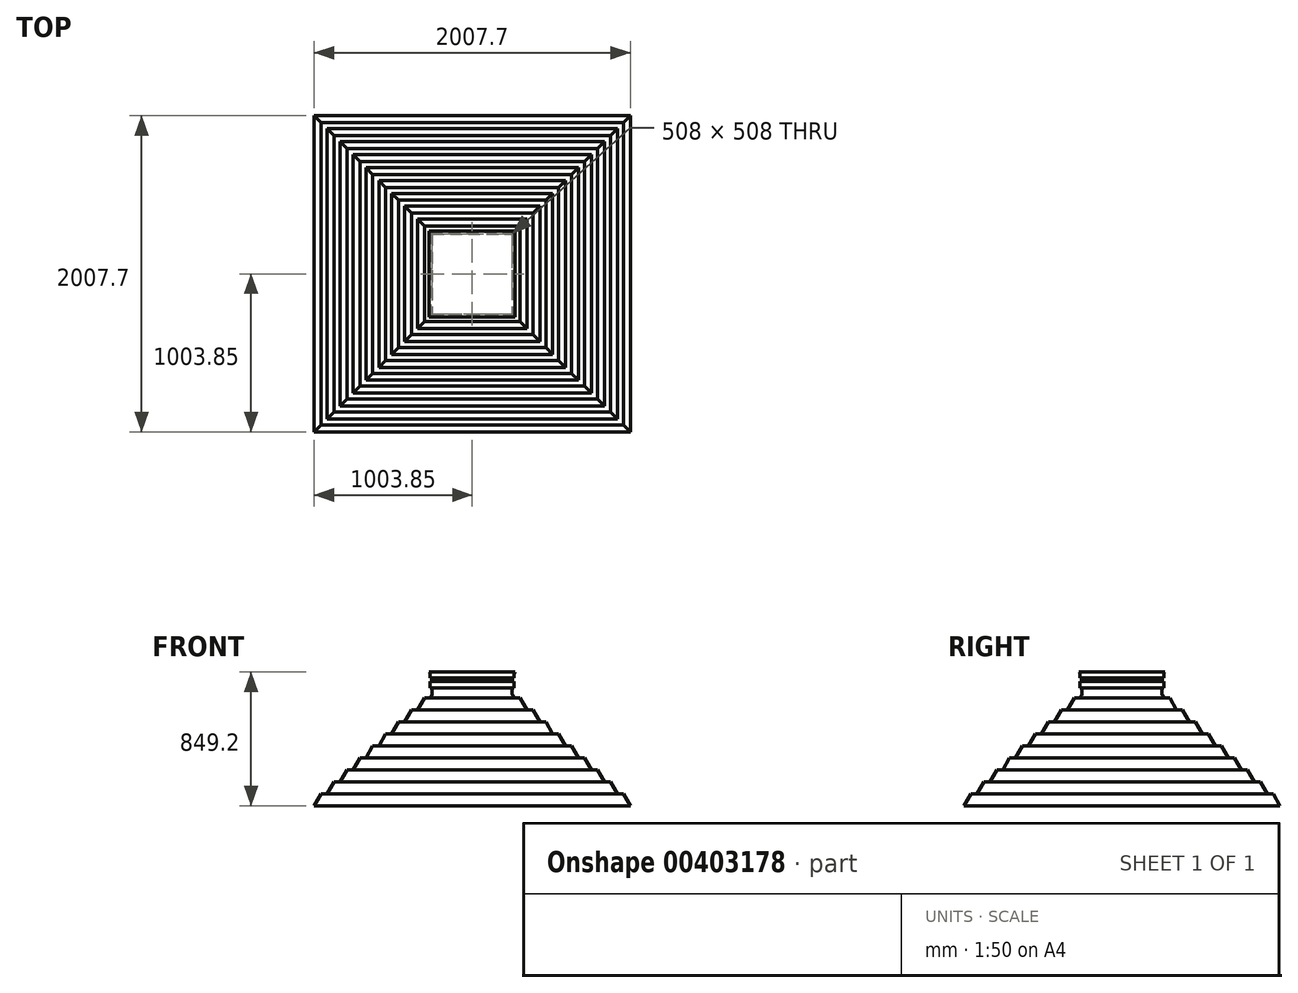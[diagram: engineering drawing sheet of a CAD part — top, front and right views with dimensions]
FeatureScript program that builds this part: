
annotation { "Feature Type Name" : "Feature", "Feature Type Description" : "" }
export const myFeature = defineFeature(function(context is Context, id is Id, definition is map)
    precondition{}
    {
        {
            var Q0;
            Q0=qCreatedBy(makeId("Front.planeOp"),FACE);
            var sketch = newSketch(context, id + "F0", { "sketchPlane" : qUnion([Q0])});
            skLineSegment(sketch, "E0", {"start": v(-254, 387.76) * mm, "end": v(-254, 363.24) * mm});
            skLineSegment(sketch, "E1", {"start": v(-265, 261.2) * mm, "end": v(265, 261.2) * mm});
            skLineSegment(sketch, "E2", {"start": v(254, 283.65) * mm, "end": v(254, 324.48) * mm});
            skLineSegment(sketch, "E3", {"start": v(-266.7, 337.4) * mm, "end": v(266.7, 337.4) * mm});
            skLineSegment(sketch, "E4", {"start": v(-266.7, 363.24) * mm, "end": v(266.7, 363.24) * mm});
            skLineSegment(sketch, "E5", {"start": v(-266.7, 354.13) * mm, "end": v(-266.7, 363.24) * mm});
            skLineSegment(sketch, "E6", {"start": v(-266.7, 350.32) * mm, "end": v(266.7, 350.32) * mm});
            skLineSegment(sketch, "E7", {"start": v(-254, 324.48) * mm, "end": v(-254, 283.65) * mm});
            skLineSegment(sketch, "E8", {"start": v(254, 363.24) * mm, "end": v(254, 387.76) * mm});
            skLineSegment(sketch, "E9", {"start": v(-266.7, 387.76) * mm, "end": v(266.7, 387.76) * mm});
            skLineSegment(sketch, "E10", {"start": v(-266.7, 387.76) * mm, "end": v(-266.7, 404.49) * mm});
            skLineSegment(sketch, "E11", {"start": v(266.7, 387.76) * mm, "end": v(266.7, 404.49) * mm});
            skLineSegment(sketch, "E12", {"start": v(-266.7, 400.68) * mm, "end": v(266.7, 400.68) * mm});
            skLineSegment(sketch, "E13", {"start": v(266.7, 404.49) * mm, "end": v(266.7, 411.9) * mm});
            skLineSegment(sketch, "E14", {"start": v(-266.7, 404.49) * mm, "end": v(-266.7, 411.9) * mm});
            skLineSegment(sketch, "E15", {"start": v(266.7, 354.13) * mm, "end": v(266.7, 363.24) * mm});
            skLineSegment(sketch, "E16", {"start": v(-255.7, 277.3) * mm, "end": v(-265, 261.2) * mm});
            skLineSegment(sketch, "E17", {"start": v(255.7, 277.3) * mm, "end": v(265, 261.2) * mm});
            skArc(sketch, "E18", {"start": v(-255.7, 277.3) * mm, "mid": v(-254.43, 280.37) * mm, "end": v(-254, 283.65) * mm});
            skArc(sketch, "E19", {"start": v(254, 283.65) * mm, "mid": v(254.43, 280.37) * mm, "end": v(255.7, 277.3) * mm});
            skLineSegment(sketch, "E20", {"start": v(0, 312) * mm, "end": v(76.2, 312) * mm});
            skLineSegment(sketch, "E21", {"start": v(76.2, 312) * mm, "end": v(76.2, 261.2) * mm});
            skLineSegment(sketch, "E22", {"start": v(0, 312) * mm, "end": v(-76.2, 312) * mm});
            skLineSegment(sketch, "E23", {"start": v(-76.2, 312) * mm, "end": v(-76.2, 261.2) * mm});
            skLineSegment(sketch, "E24", {"start": v(-38.1, 305.65) * mm, "end": v(-38.1, 261.2) * mm});
            skLineSegment(sketch, "E25", {"start": v(38.1, 305.65) * mm, "end": v(38.1, 261.2) * mm});
            skLineSegment(sketch, "E26", {"start": v(50.8, 305.65) * mm, "end": v(50.8, 261.2) * mm});
            skLineSegment(sketch, "E27", {"start": v(-50.8, 305.65) * mm, "end": v(-50.8, 261.2) * mm});
            skLineSegment(sketch, "E28", {"start": v(-303.1, 261.2) * mm, "end": v(-265, 261.2) * mm});
            skLineSegment(sketch, "E29", {"start": v(303.1, 261.2) * mm, "end": v(265, 261.2) * mm});
            skLineSegment(sketch, "E30", {"start": v(-549.38, 32.6) * mm, "end": v(-101.6, 32.6) * mm});
            skLineSegment(sketch, "E31", {"start": v(-631.47, -43.6) * mm, "end": v(-101.6, -43.6) * mm});
            skLineSegment(sketch, "E32", {"start": v(-303.1, 261.2) * mm, "end": v(-347.1, 185) * mm});
            skLineSegment(sketch, "E33", {"start": v(-385.2, 185) * mm, "end": v(-429.19, 108.8) * mm});
            skLineSegment(sketch, "E34", {"start": v(-467.29, 108.8) * mm, "end": v(-511.28, 32.6) * mm});
            skLineSegment(sketch, "E35", {"start": v(-549.38, 32.6) * mm, "end": v(-593.37, -43.6) * mm});
            skLineSegment(sketch, "E36", {"start": v(-631.47, -43.6) * mm, "end": v(-675.47, -119.8) * mm});
            skLineSegment(sketch, "E37", {"start": v(-713.57, -119.8) * mm, "end": v(-757.56, -196) * mm});
            skLineSegment(sketch, "E38", {"start": v(-795.66, -196) * mm, "end": v(-839.66, -272.2) * mm});
            skLineSegment(sketch, "E39", {"start": v(-877.76, -272.2) * mm, "end": v(-921.75, -348.4) * mm});
            skLineSegment(sketch, "E40", {"start": v(-959.85, -348.4) * mm, "end": v(-1003.85, -424.6) * mm});
            skLineSegment(sketch, "E41", {"start": v(303.1, 261.2) * mm, "end": v(347.1, 185) * mm});
            skLineSegment(sketch, "E42", {"start": v(385.2, 185) * mm, "end": v(429.19, 108.8) * mm});
            skLineSegment(sketch, "E43", {"start": v(467.29, 108.8) * mm, "end": v(511.28, 32.6) * mm});
            skLineSegment(sketch, "E44", {"start": v(549.38, 32.6) * mm, "end": v(593.37, -43.6) * mm});
            skLineSegment(sketch, "E45", {"start": v(631.47, -43.6) * mm, "end": v(675.47, -119.8) * mm});
            skLineSegment(sketch, "E46", {"start": v(713.57, -119.8) * mm, "end": v(757.56, -196) * mm});
            skLineSegment(sketch, "E47", {"start": v(795.66, -196) * mm, "end": v(839.66, -272.2) * mm});
            skLineSegment(sketch, "E48", {"start": v(877.76, -272.2) * mm, "end": v(921.75, -348.4) * mm});
            skLineSegment(sketch, "E49", {"start": v(959.85, -348.4) * mm, "end": v(1003.85, -424.6) * mm});
            skLineSegment(sketch, "E50", {"start": v(-959.85, -348.4) * mm, "end": v(-101.6, -348.4) * mm});
            skLineSegment(sketch, "E51", {"start": v(-795.66, -196) * mm, "end": v(-101.6, -196) * mm});
            skLineSegment(sketch, "E52", {"start": v(-877.76, -272.2) * mm, "end": v(-101.6, -272.2) * mm});
            skLineSegment(sketch, "E53", {"start": v(-713.57, -119.8) * mm, "end": v(-101.6, -119.8) * mm});
            skLineSegment(sketch, "E54", {"start": v(-385.2, 185) * mm, "end": v(-101.6, 185) * mm});
            skLineSegment(sketch, "E55", {"start": v(-467.29, 108.8) * mm, "end": v(-101.6, 108.8) * mm});
            skLineSegment(sketch, "E56", {"start": v(-870, -399.2) * mm, "end": v(-870, -361.1) * mm});
            skLineSegment(sketch, "E57", {"start": v(-736.15, -399.2) * mm, "end": v(-736.15, -361.1) * mm});
            skLineSegment(sketch, "E58", {"start": v(-602.3, -399.2) * mm, "end": v(-602.3, -361.1) * mm});
            skLineSegment(sketch, "E59", {"start": v(-870, -361.1) * mm, "end": v(-736.15, -361.1) * mm});
            skLineSegment(sketch, "E60", {"start": v(-989.18, -399.2) * mm, "end": v(-870, -399.2) * mm});
            skLineSegment(sketch, "E61", {"start": v(-736.15, -399.2) * mm, "end": v(-602.3, -399.2) * mm});
            skLineSegment(sketch, "E62", {"start": v(-602.3, -361.1) * mm, "end": v(-468.46, -361.1) * mm});
            skLineSegment(sketch, "E63", {"start": v(-468.46, -399.2) * mm, "end": v(-334.62, -399.2) * mm});
            skLineSegment(sketch, "E64", {"start": v(-334.62, -361.1) * mm, "end": v(-200.77, -361.1) * mm});
            skLineSegment(sketch, "E65", {"start": v(101.6, -399.2) * mm, "end": v(200.77, -399.2) * mm});
            skLineSegment(sketch, "E66", {"start": v(200.77, -361.1) * mm, "end": v(334.62, -361.1) * mm});
            skLineSegment(sketch, "E67", {"start": v(870, -399.2) * mm, "end": v(989.18, -399.2) * mm});
            skLineSegment(sketch, "E68", {"start": v(736.15, -361.1) * mm, "end": v(870, -361.1) * mm});
            skLineSegment(sketch, "E69", {"start": v(602.3, -399.2) * mm, "end": v(736.15, -399.2) * mm});
            skLineSegment(sketch, "E70", {"start": v(468.46, -361.1) * mm, "end": v(602.3, -361.1) * mm});
            skLineSegment(sketch, "E71", {"start": v(-1003.85, -424.6) * mm, "end": v(76.2, -424.6) * mm});
            skLineSegment(sketch, "E72", {"start": v(-468.46, -399.2) * mm, "end": v(-468.46, -361.1) * mm});
            skLineSegment(sketch, "E73", {"start": v(-334.62, -399.2) * mm, "end": v(-334.62, -361.1) * mm});
            skLineSegment(sketch, "E74", {"start": v(-200.77, -399.2) * mm, "end": v(-200.77, -361.1) * mm});
            skLineSegment(sketch, "E75", {"start": v(-200.77, -399.2) * mm, "end": v(-101.6, -399.2) * mm});
            skLineSegment(sketch, "E76", {"start": v(200.77, -399.2) * mm, "end": v(200.77, -361.1) * mm});
            skLineSegment(sketch, "E77", {"start": v(334.62, -399.2) * mm, "end": v(468.46, -399.2) * mm});
            skLineSegment(sketch, "E78", {"start": v(334.62, -399.2) * mm, "end": v(334.62, -361.1) * mm});
            skLineSegment(sketch, "E79", {"start": v(468.46, -399.2) * mm, "end": v(468.46, -361.1) * mm});
            skLineSegment(sketch, "E80", {"start": v(602.3, -399.2) * mm, "end": v(602.3, -361.1) * mm});
            skLineSegment(sketch, "E81", {"start": v(736.15, -399.2) * mm, "end": v(736.15, -361.1) * mm});
            skLineSegment(sketch, "E82", {"start": v(870, -361.1) * mm, "end": v(870, -399.2) * mm});
            skLineSegment(sketch, "E83", {"start": v(101.6, -348.4) * mm, "end": v(959.85, -348.4) * mm});
            skLineSegment(sketch, "E84", {"start": v(101.6, -272.2) * mm, "end": v(877.76, -272.2) * mm});
            skLineSegment(sketch, "E85", {"start": v(101.6, -196) * mm, "end": v(795.66, -196) * mm});
            skLineSegment(sketch, "E86", {"start": v(101.6, -119.8) * mm, "end": v(713.57, -119.8) * mm});
            skLineSegment(sketch, "E87", {"start": v(101.6, -43.6) * mm, "end": v(631.47, -43.6) * mm});
            skLineSegment(sketch, "E88", {"start": v(101.6, 32.6) * mm, "end": v(549.38, 32.6) * mm});
            skLineSegment(sketch, "E89", {"start": v(101.6, 108.8) * mm, "end": v(467.29, 108.8) * mm});
            skLineSegment(sketch, "E90", {"start": v(101.6, 185) * mm, "end": v(385.2, 185) * mm});
            skLineSegment(sketch, "E91", {"start": v(-292.38, 248.5) * mm, "end": v(-247.41, 248.5) * mm});
            skLineSegment(sketch, "E92", {"start": v(-202.44, 248.5) * mm, "end": v(-157.47, 248.5) * mm});
            skLineSegment(sketch, "E93", {"start": v(-112.5, 248.5) * mm, "end": v(-101.6, 248.5) * mm});
            skLineSegment(sketch, "E94", {"start": v(101.6, 248.5) * mm, "end": v(112.37, 248.5) * mm});
            skLineSegment(sketch, "E95", {"start": v(157.34, 248.5) * mm, "end": v(202.31, 248.5) * mm});
            skLineSegment(sketch, "E96", {"start": v(247.28, 248.5) * mm, "end": v(292.26, 248.5) * mm});
            skLineSegment(sketch, "E97", {"start": v(-292.38, 210.4) * mm, "end": v(-292.38, 248.5) * mm});
            skLineSegment(sketch, "E98", {"start": v(-247.41, 210.4) * mm, "end": v(-247.41, 248.5) * mm});
            skLineSegment(sketch, "E99", {"start": v(-202.44, 210.4) * mm, "end": v(-202.44, 248.5) * mm});
            skLineSegment(sketch, "E100", {"start": v(-157.47, 210.4) * mm, "end": v(-157.47, 248.5) * mm});
            skLineSegment(sketch, "E101", {"start": v(-112.5, 210.4) * mm, "end": v(-112.5, 248.5) * mm});
            skLineSegment(sketch, "E102", {"start": v(112.37, 210.4) * mm, "end": v(112.37, 248.5) * mm});
            skLineSegment(sketch, "E103", {"start": v(157.34, 210.4) * mm, "end": v(157.34, 248.5) * mm});
            skLineSegment(sketch, "E104", {"start": v(202.31, 210.4) * mm, "end": v(202.31, 248.5) * mm});
            skLineSegment(sketch, "E105", {"start": v(247.28, 210.4) * mm, "end": v(247.28, 248.5) * mm});
            skLineSegment(sketch, "E106", {"start": v(-332.43, 210.4) * mm, "end": v(-292.38, 210.4) * mm});
            skLineSegment(sketch, "E107", {"start": v(-247.41, 210.4) * mm, "end": v(-202.44, 210.4) * mm});
            skLineSegment(sketch, "E108", {"start": v(-157.47, 210.4) * mm, "end": v(-112.5, 210.4) * mm});
            skLineSegment(sketch, "E109", {"start": v(202.31, 210.4) * mm, "end": v(247.28, 210.4) * mm});
            skLineSegment(sketch, "E110", {"start": v(292.26, 210.4) * mm, "end": v(332.3, 210.4) * mm});
            skLineSegment(sketch, "E111", {"start": v(112.37, 210.4) * mm, "end": v(157.34, 210.4) * mm});
            skLineSegment(sketch, "E112", {"start": v(292.26, 248.5) * mm, "end": v(292.26, 210.4) * mm});
            skLineSegment(sketch, "E113", {"start": v(-364.59, 172.3) * mm, "end": v(-308.5, 172.3) * mm});
            skLineSegment(sketch, "E114", {"start": v(-252.42, 172.3) * mm, "end": v(-196.34, 172.3) * mm});
            skLineSegment(sketch, "E115", {"start": v(-140.26, 172.3) * mm, "end": v(-101.6, 172.3) * mm});
            skLineSegment(sketch, "E116", {"start": v(101.6, 172.3) * mm, "end": v(140.15, 172.3) * mm});
            skLineSegment(sketch, "E117", {"start": v(196.23, 172.3) * mm, "end": v(252.31, 172.3) * mm});
            skLineSegment(sketch, "E118", {"start": v(308.4, 172.3) * mm, "end": v(364.47, 172.3) * mm});
            skLineSegment(sketch, "E119", {"start": v(-364.59, 134.2) * mm, "end": v(-364.59, 172.3) * mm});
            skLineSegment(sketch, "E120", {"start": v(-308.5, 134.2) * mm, "end": v(-308.5, 172.3) * mm});
            skLineSegment(sketch, "E121", {"start": v(-252.42, 134.2) * mm, "end": v(-252.42, 172.3) * mm});
            skLineSegment(sketch, "E122", {"start": v(-196.34, 134.2) * mm, "end": v(-196.34, 172.3) * mm});
            skLineSegment(sketch, "E123", {"start": v(-140.26, 134.2) * mm, "end": v(-140.26, 172.3) * mm});
            skLineSegment(sketch, "E124", {"start": v(140.15, 134.2) * mm, "end": v(140.15, 172.3) * mm});
            skLineSegment(sketch, "E125", {"start": v(196.23, 134.2) * mm, "end": v(196.23, 172.3) * mm});
            skLineSegment(sketch, "E126", {"start": v(252.31, 134.2) * mm, "end": v(252.31, 172.3) * mm});
            skLineSegment(sketch, "E127", {"start": v(308.4, 134.2) * mm, "end": v(308.4, 172.3) * mm});
            skLineSegment(sketch, "E128", {"start": v(-414.52, 134.2) * mm, "end": v(-364.59, 134.2) * mm});
            skLineSegment(sketch, "E129", {"start": v(-308.5, 134.2) * mm, "end": v(-252.42, 134.2) * mm});
            skLineSegment(sketch, "E130", {"start": v(-196.34, 134.2) * mm, "end": v(-140.26, 134.2) * mm});
            skLineSegment(sketch, "E131", {"start": v(252.31, 134.2) * mm, "end": v(308.4, 134.2) * mm});
            skLineSegment(sketch, "E132", {"start": v(364.47, 134.2) * mm, "end": v(414.41, 134.2) * mm});
            skLineSegment(sketch, "E133", {"start": v(140.15, 134.2) * mm, "end": v(196.23, 134.2) * mm});
            skLineSegment(sketch, "E134", {"start": v(364.47, 172.3) * mm, "end": v(364.47, 134.2) * mm});
            skLineSegment(sketch, "E135", {"start": v(-436.79, 96.1) * mm, "end": v(-369.6, 96.1) * mm});
            skLineSegment(sketch, "E136", {"start": v(-302.4, 96.1) * mm, "end": v(-235.21, 96.1) * mm});
            skLineSegment(sketch, "E137", {"start": v(-168.02, 96.1) * mm, "end": v(-101.6, 96.1) * mm});
            skLineSegment(sketch, "E138", {"start": v(101.6, 96.1) * mm, "end": v(167.93, 96.1) * mm});
            skLineSegment(sketch, "E139", {"start": v(235.12, 96.1) * mm, "end": v(302.31, 96.1) * mm});
            skLineSegment(sketch, "E140", {"start": v(369.5, 96.1) * mm, "end": v(436.7, 96.1) * mm});
            skLineSegment(sketch, "E141", {"start": v(-436.79, 58) * mm, "end": v(-436.79, 96.1) * mm});
            skLineSegment(sketch, "E142", {"start": v(-369.6, 58) * mm, "end": v(-369.6, 96.1) * mm});
            skLineSegment(sketch, "E143", {"start": v(-302.4, 58) * mm, "end": v(-302.4, 96.1) * mm});
            skLineSegment(sketch, "E144", {"start": v(-235.21, 58) * mm, "end": v(-235.21, 96.1) * mm});
            skLineSegment(sketch, "E145", {"start": v(-168.02, 58) * mm, "end": v(-168.02, 96.1) * mm});
            skLineSegment(sketch, "E146", {"start": v(167.93, 58) * mm, "end": v(167.93, 96.1) * mm});
            skLineSegment(sketch, "E147", {"start": v(235.12, 58) * mm, "end": v(235.12, 96.1) * mm});
            skLineSegment(sketch, "E148", {"start": v(302.31, 58) * mm, "end": v(302.31, 96.1) * mm});
            skLineSegment(sketch, "E149", {"start": v(369.5, 58) * mm, "end": v(369.5, 96.1) * mm});
            skLineSegment(sketch, "E150", {"start": v(-496.62, 58) * mm, "end": v(-436.79, 58) * mm});
            skLineSegment(sketch, "E151", {"start": v(-369.6, 58) * mm, "end": v(-302.4, 58) * mm});
            skLineSegment(sketch, "E152", {"start": v(-235.21, 58) * mm, "end": v(-168.02, 58) * mm});
            skLineSegment(sketch, "E153", {"start": v(302.31, 58) * mm, "end": v(369.5, 58) * mm});
            skLineSegment(sketch, "E154", {"start": v(436.7, 58) * mm, "end": v(496.52, 58) * mm});
            skLineSegment(sketch, "E155", {"start": v(167.93, 58) * mm, "end": v(235.12, 58) * mm});
            skLineSegment(sketch, "E156", {"start": v(436.7, 96.1) * mm, "end": v(436.7, 58) * mm});
            skLineSegment(sketch, "E157", {"start": v(-508.99, 19.9) * mm, "end": v(-430.69, 19.9) * mm});
            skLineSegment(sketch, "E158", {"start": v(-352.39, 19.9) * mm, "end": v(-274.09, 19.9) * mm});
            skLineSegment(sketch, "E159", {"start": v(-195.79, 19.9) * mm, "end": v(-117.49, 19.9) * mm});
            skLineSegment(sketch, "E160", {"start": v(117.41, 19.9) * mm, "end": v(195.71, 19.9) * mm});
            skLineSegment(sketch, "E161", {"start": v(274.01, 19.9) * mm, "end": v(352.31, 19.9) * mm});
            skLineSegment(sketch, "E162", {"start": v(430.61, 19.9) * mm, "end": v(508.91, 19.9) * mm});
            skLineSegment(sketch, "E163", {"start": v(-508.99, -18.2) * mm, "end": v(-508.99, 19.9) * mm});
            skLineSegment(sketch, "E164", {"start": v(-430.69, -18.2) * mm, "end": v(-430.69, 19.9) * mm});
            skLineSegment(sketch, "E165", {"start": v(-352.39, -18.2) * mm, "end": v(-352.39, 19.9) * mm});
            skLineSegment(sketch, "E166", {"start": v(-274.09, -18.2) * mm, "end": v(-274.09, 19.9) * mm});
            skLineSegment(sketch, "E167", {"start": v(-195.79, -18.2) * mm, "end": v(-195.79, 19.9) * mm});
            skLineSegment(sketch, "E168", {"start": v(-117.49, -18.2) * mm, "end": v(-117.49, 19.9) * mm});
            skLineSegment(sketch, "E169", {"start": v(117.41, -18.2) * mm, "end": v(117.41, 19.9) * mm});
            skLineSegment(sketch, "E170", {"start": v(195.71, -18.2) * mm, "end": v(195.71, 19.9) * mm});
            skLineSegment(sketch, "E171", {"start": v(274.01, -18.2) * mm, "end": v(274.01, 19.9) * mm});
            skLineSegment(sketch, "E172", {"start": v(352.31, -18.2) * mm, "end": v(352.31, 19.9) * mm});
            skLineSegment(sketch, "E173", {"start": v(430.61, -18.2) * mm, "end": v(430.61, 19.9) * mm});
            skLineSegment(sketch, "E174", {"start": v(-578.71, -18.2) * mm, "end": v(-508.99, -18.2) * mm});
            skLineSegment(sketch, "E175", {"start": v(-430.69, -18.2) * mm, "end": v(-352.39, -18.2) * mm});
            skLineSegment(sketch, "E176", {"start": v(-274.09, -18.2) * mm, "end": v(-195.79, -18.2) * mm});
            skLineSegment(sketch, "E177", {"start": v(-117.49, -18.2) * mm, "end": v(-101.6, -18.2) * mm});
            skLineSegment(sketch, "E178", {"start": v(101.6, -18.2) * mm, "end": v(117.41, -18.2) * mm});
            skLineSegment(sketch, "E179", {"start": v(352.31, -18.2) * mm, "end": v(430.61, -18.2) * mm});
            skLineSegment(sketch, "E180", {"start": v(508.91, -18.2) * mm, "end": v(578.63, -18.2) * mm});
            skLineSegment(sketch, "E181", {"start": v(195.71, -18.2) * mm, "end": v(274.01, -18.2) * mm});
            skLineSegment(sketch, "E182", {"start": v(508.91, 19.9) * mm, "end": v(508.91, -18.2) * mm});
            skLineSegment(sketch, "E183", {"start": v(-581.2, -56.3) * mm, "end": v(-491.78, -56.3) * mm});
            skLineSegment(sketch, "E184", {"start": v(-402.37, -56.3) * mm, "end": v(-312.96, -56.3) * mm});
            skLineSegment(sketch, "E185", {"start": v(-223.55, -56.3) * mm, "end": v(-134.15, -56.3) * mm});
            skLineSegment(sketch, "E186", {"start": v(134.08, -56.3) * mm, "end": v(223.5, -56.3) * mm});
            skLineSegment(sketch, "E187", {"start": v(312.9, -56.3) * mm, "end": v(402.3, -56.3) * mm});
            skLineSegment(sketch, "E188", {"start": v(491.72, -56.3) * mm, "end": v(581.13, -56.3) * mm});
            skLineSegment(sketch, "E189", {"start": v(-581.2, -94.4) * mm, "end": v(-581.2, -56.3) * mm});
            skLineSegment(sketch, "E190", {"start": v(-491.78, -94.4) * mm, "end": v(-491.78, -56.3) * mm});
            skLineSegment(sketch, "E191", {"start": v(-402.37, -94.4) * mm, "end": v(-402.37, -56.3) * mm});
            skLineSegment(sketch, "E192", {"start": v(-312.96, -94.4) * mm, "end": v(-312.96, -56.3) * mm});
            skLineSegment(sketch, "E193", {"start": v(-223.55, -94.4) * mm, "end": v(-223.55, -56.3) * mm});
            skLineSegment(sketch, "E194", {"start": v(-134.15, -94.4) * mm, "end": v(-134.15, -56.3) * mm});
            skLineSegment(sketch, "E195", {"start": v(134.08, -94.4) * mm, "end": v(134.08, -56.3) * mm});
            skLineSegment(sketch, "E196", {"start": v(223.5, -94.4) * mm, "end": v(223.5, -56.3) * mm});
            skLineSegment(sketch, "E197", {"start": v(312.9, -94.4) * mm, "end": v(312.9, -56.3) * mm});
            skLineSegment(sketch, "E198", {"start": v(402.3, -94.4) * mm, "end": v(402.3, -56.3) * mm});
            skLineSegment(sketch, "E199", {"start": v(491.72, -94.4) * mm, "end": v(491.72, -56.3) * mm});
            skLineSegment(sketch, "E200", {"start": v(-660.8, -94.4) * mm, "end": v(-581.2, -94.4) * mm});
            skLineSegment(sketch, "E201", {"start": v(-491.78, -94.4) * mm, "end": v(-402.37, -94.4) * mm});
            skLineSegment(sketch, "E202", {"start": v(-312.96, -94.4) * mm, "end": v(-223.55, -94.4) * mm});
            skLineSegment(sketch, "E203", {"start": v(-134.15, -94.4) * mm, "end": v(-101.6, -94.4) * mm});
            skLineSegment(sketch, "E204", {"start": v(101.6, -94.4) * mm, "end": v(134.08, -94.4) * mm});
            skLineSegment(sketch, "E205", {"start": v(402.3, -94.4) * mm, "end": v(491.72, -94.4) * mm});
            skLineSegment(sketch, "E206", {"start": v(581.13, -94.4) * mm, "end": v(660.74, -94.4) * mm});
            skLineSegment(sketch, "E207", {"start": v(223.5, -94.4) * mm, "end": v(312.9, -94.4) * mm});
            skLineSegment(sketch, "E208", {"start": v(581.13, -56.3) * mm, "end": v(581.13, -94.4) * mm});
            skLineSegment(sketch, "E209", {"start": v(-653.4, -132.5) * mm, "end": v(-552.87, -132.5) * mm});
            skLineSegment(sketch, "E210", {"start": v(-452.36, -132.5) * mm, "end": v(-351.84, -132.5) * mm});
            skLineSegment(sketch, "E211", {"start": v(-251.32, -132.5) * mm, "end": v(-150.8, -132.5) * mm});
            skLineSegment(sketch, "E212", {"start": v(150.75, -132.5) * mm, "end": v(251.27, -132.5) * mm});
            skLineSegment(sketch, "E213", {"start": v(351.8, -132.5) * mm, "end": v(452.3, -132.5) * mm});
            skLineSegment(sketch, "E214", {"start": v(552.83, -132.5) * mm, "end": v(653.35, -132.5) * mm});
            skLineSegment(sketch, "E215", {"start": v(-653.4, -170.6) * mm, "end": v(-653.4, -132.5) * mm});
            skLineSegment(sketch, "E216", {"start": v(-552.87, -170.6) * mm, "end": v(-552.87, -132.5) * mm});
            skLineSegment(sketch, "E217", {"start": v(-452.36, -170.6) * mm, "end": v(-452.36, -132.5) * mm});
            skLineSegment(sketch, "E218", {"start": v(-351.84, -170.6) * mm, "end": v(-351.84, -132.5) * mm});
            skLineSegment(sketch, "E219", {"start": v(-251.32, -170.6) * mm, "end": v(-251.32, -132.5) * mm});
            skLineSegment(sketch, "E220", {"start": v(-150.8, -170.6) * mm, "end": v(-150.8, -132.5) * mm});
            skLineSegment(sketch, "E221", {"start": v(150.75, -170.6) * mm, "end": v(150.75, -132.5) * mm});
            skLineSegment(sketch, "E222", {"start": v(251.27, -170.6) * mm, "end": v(251.27, -132.5) * mm});
            skLineSegment(sketch, "E223", {"start": v(351.8, -170.6) * mm, "end": v(351.8, -132.5) * mm});
            skLineSegment(sketch, "E224", {"start": v(452.3, -170.6) * mm, "end": v(452.3, -132.5) * mm});
            skLineSegment(sketch, "E225", {"start": v(552.83, -170.6) * mm, "end": v(552.83, -132.5) * mm});
            skLineSegment(sketch, "E226", {"start": v(-742.9, -170.6) * mm, "end": v(-653.4, -170.6) * mm});
            skLineSegment(sketch, "E227", {"start": v(-552.87, -170.6) * mm, "end": v(-452.36, -170.6) * mm});
            skLineSegment(sketch, "E228", {"start": v(-351.84, -170.6) * mm, "end": v(-251.32, -170.6) * mm});
            skLineSegment(sketch, "E229", {"start": v(-150.8, -170.6) * mm, "end": v(-101.6, -170.6) * mm});
            skLineSegment(sketch, "E230", {"start": v(101.6, -170.6) * mm, "end": v(150.75, -170.6) * mm});
            skLineSegment(sketch, "E231", {"start": v(452.3, -170.6) * mm, "end": v(552.83, -170.6) * mm});
            skLineSegment(sketch, "E232", {"start": v(653.35, -170.6) * mm, "end": v(742.85, -170.6) * mm});
            skLineSegment(sketch, "E233", {"start": v(251.27, -170.6) * mm, "end": v(351.8, -170.6) * mm});
            skLineSegment(sketch, "E234", {"start": v(653.35, -132.5) * mm, "end": v(653.35, -170.6) * mm});
            skLineSegment(sketch, "E235", {"start": v(-725.6, -208.7) * mm, "end": v(-613.97, -208.7) * mm});
            skLineSegment(sketch, "E236", {"start": v(-502.34, -208.7) * mm, "end": v(-390.71, -208.7) * mm});
            skLineSegment(sketch, "E237", {"start": v(-279.08, -208.7) * mm, "end": v(-167.46, -208.7) * mm});
            skLineSegment(sketch, "E238", {"start": v(167.43, -208.7) * mm, "end": v(279.05, -208.7) * mm});
            skLineSegment(sketch, "E239", {"start": v(390.68, -208.7) * mm, "end": v(502.3, -208.7) * mm});
            skLineSegment(sketch, "E240", {"start": v(613.94, -208.7) * mm, "end": v(725.56, -208.7) * mm});
            skLineSegment(sketch, "E241", {"start": v(-725.6, -246.8) * mm, "end": v(-725.6, -208.7) * mm});
            skLineSegment(sketch, "E242", {"start": v(-613.97, -246.8) * mm, "end": v(-613.97, -208.7) * mm});
            skLineSegment(sketch, "E243", {"start": v(-502.34, -246.8) * mm, "end": v(-502.34, -208.7) * mm});
            skLineSegment(sketch, "E244", {"start": v(-390.71, -246.8) * mm, "end": v(-390.71, -208.7) * mm});
            skLineSegment(sketch, "E245", {"start": v(-279.08, -246.8) * mm, "end": v(-279.08, -208.7) * mm});
            skLineSegment(sketch, "E246", {"start": v(-167.46, -246.8) * mm, "end": v(-167.46, -208.7) * mm});
            skLineSegment(sketch, "E247", {"start": v(167.43, -246.8) * mm, "end": v(167.43, -208.7) * mm});
            skLineSegment(sketch, "E248", {"start": v(279.05, -246.8) * mm, "end": v(279.05, -208.7) * mm});
            skLineSegment(sketch, "E249", {"start": v(390.68, -246.8) * mm, "end": v(390.68, -208.7) * mm});
            skLineSegment(sketch, "E250", {"start": v(502.3, -246.8) * mm, "end": v(502.3, -208.7) * mm});
            skLineSegment(sketch, "E251", {"start": v(613.94, -246.8) * mm, "end": v(613.94, -208.7) * mm});
            skLineSegment(sketch, "E252", {"start": v(-825, -246.8) * mm, "end": v(-725.6, -246.8) * mm});
            skLineSegment(sketch, "E253", {"start": v(-613.97, -246.8) * mm, "end": v(-502.34, -246.8) * mm});
            skLineSegment(sketch, "E254", {"start": v(-390.71, -246.8) * mm, "end": v(-279.08, -246.8) * mm});
            skLineSegment(sketch, "E255", {"start": v(-167.46, -246.8) * mm, "end": v(-101.6, -246.8) * mm});
            skLineSegment(sketch, "E256", {"start": v(101.6, -246.8) * mm, "end": v(167.43, -246.8) * mm});
            skLineSegment(sketch, "E257", {"start": v(502.3, -246.8) * mm, "end": v(613.94, -246.8) * mm});
            skLineSegment(sketch, "E258", {"start": v(725.56, -246.8) * mm, "end": v(824.96, -246.8) * mm});
            skLineSegment(sketch, "E259", {"start": v(279.05, -246.8) * mm, "end": v(390.68, -246.8) * mm});
            skLineSegment(sketch, "E260", {"start": v(725.56, -208.7) * mm, "end": v(725.56, -246.8) * mm});
            skLineSegment(sketch, "E261", {"start": v(-797.8, -284.9) * mm, "end": v(-675.06, -284.9) * mm});
            skLineSegment(sketch, "E262", {"start": v(-552.32, -284.9) * mm, "end": v(-429.59, -284.9) * mm});
            skLineSegment(sketch, "E263", {"start": v(-306.85, -284.9) * mm, "end": v(-184.11, -284.9) * mm});
            skLineSegment(sketch, "E264", {"start": v(184.1, -284.9) * mm, "end": v(306.83, -284.9) * mm});
            skLineSegment(sketch, "E265", {"start": v(429.57, -284.9) * mm, "end": v(552.3, -284.9) * mm});
            skLineSegment(sketch, "E266", {"start": v(675.04, -284.9) * mm, "end": v(797.78, -284.9) * mm});
            skLineSegment(sketch, "E267", {"start": v(-797.8, -323) * mm, "end": v(-797.8, -284.9) * mm});
            skLineSegment(sketch, "E268", {"start": v(-675.06, -323) * mm, "end": v(-675.06, -284.9) * mm});
            skLineSegment(sketch, "E269", {"start": v(-552.32, -323) * mm, "end": v(-552.32, -284.9) * mm});
            skLineSegment(sketch, "E270", {"start": v(-429.59, -323) * mm, "end": v(-429.59, -284.9) * mm});
            skLineSegment(sketch, "E271", {"start": v(-306.85, -323) * mm, "end": v(-306.85, -284.9) * mm});
            skLineSegment(sketch, "E272", {"start": v(-184.11, -323) * mm, "end": v(-184.11, -284.9) * mm});
            skLineSegment(sketch, "E273", {"start": v(184.1, -323) * mm, "end": v(184.1, -284.9) * mm});
            skLineSegment(sketch, "E274", {"start": v(306.83, -323) * mm, "end": v(306.83, -284.9) * mm});
            skLineSegment(sketch, "E275", {"start": v(429.57, -323) * mm, "end": v(429.57, -284.9) * mm});
            skLineSegment(sketch, "E276", {"start": v(552.3, -323) * mm, "end": v(552.3, -284.9) * mm});
            skLineSegment(sketch, "E277", {"start": v(675.04, -323) * mm, "end": v(675.04, -284.9) * mm});
            skLineSegment(sketch, "E278", {"start": v(-907.09, -323) * mm, "end": v(-797.8, -323) * mm});
            skLineSegment(sketch, "E279", {"start": v(-675.06, -323) * mm, "end": v(-552.32, -323) * mm});
            skLineSegment(sketch, "E280", {"start": v(-429.59, -323) * mm, "end": v(-306.85, -323) * mm});
            skLineSegment(sketch, "E281", {"start": v(-184.11, -323) * mm, "end": v(-101.6, -323) * mm});
            skLineSegment(sketch, "E282", {"start": v(101.6, -323) * mm, "end": v(184.1, -323) * mm});
            skLineSegment(sketch, "E283", {"start": v(552.3, -323) * mm, "end": v(675.04, -323) * mm});
            skLineSegment(sketch, "E284", {"start": v(797.78, -323) * mm, "end": v(907.07, -323) * mm});
            skLineSegment(sketch, "E285", {"start": v(306.83, -323) * mm, "end": v(429.57, -323) * mm});
            skLineSegment(sketch, "E286", {"start": v(797.78, -284.9) * mm, "end": v(797.78, -323) * mm});
            skLineSegment(sketch, "E287", {"start": v(-57.15, 312) * mm, "end": v(-57.15, 305.65) * mm});
            skLineSegment(sketch, "E288", {"start": v(-31.75, 312) * mm, "end": v(-31.75, 305.65) * mm});
            skLineSegment(sketch, "E289", {"start": v(31.75, 312) * mm, "end": v(31.75, 305.65) * mm});
            skLineSegment(sketch, "E290", {"start": v(57.15, 312) * mm, "end": v(57.15, 305.65) * mm});
            skLineSegment(sketch, "E291", {"start": v(38.1, 305.65) * mm, "end": v(31.75, 305.65) * mm});
            skLineSegment(sketch, "E292", {"start": v(-50.8, 305.65) * mm, "end": v(-57.15, 305.65) * mm});
            skLineSegment(sketch, "E293", {"start": v(57.15, 305.65) * mm, "end": v(50.8, 305.65) * mm});
            skLineSegment(sketch, "E294", {"start": v(-31.75, 305.65) * mm, "end": v(-38.1, 305.65) * mm});
            skLineSegment(sketch, "E295", {"start": v(-267.55, 415.07) * mm, "end": v(-273.05, 424.6) * mm});
            skLineSegment(sketch, "E296", {"start": v(267.55, 415.07) * mm, "end": v(273.05, 424.6) * mm});
            skLineSegment(sketch, "E297", {"start": v(273.05, 424.6) * mm, "end": v(-273.05, 424.6) * mm});
            skLineSegment(sketch, "E298", {"start": v(-266.7, 324.48) * mm, "end": v(266.7, 324.48) * mm});
            skLineSegment(sketch, "E299", {"start": v(-266.7, 354.13) * mm, "end": v(-266.7, 324.48) * mm});
            skLineSegment(sketch, "E300", {"start": v(-23.24, 381.85) * mm, "end": v(23.24, 381.85) * mm});
            skLineSegment(sketch, "E301", {"start": v(23.24, 381.85) * mm, "end": v(23.24, 369.15) * mm});
            skLineSegment(sketch, "E302", {"start": v(23.24, 369.15) * mm, "end": v(-23.24, 369.15) * mm});
            skLineSegment(sketch, "E303", {"start": v(-23.24, 381.85) * mm, "end": v(-23.24, 369.15) * mm});
            skLineSegment(sketch, "E304", {"start": v(180.6, 369.15) * mm, "end": v(180.6, 381.85) * mm});
            skLineSegment(sketch, "E305", {"start": v(-180.6, 381.85) * mm, "end": v(-180.6, 369.15) * mm});
            skLineSegment(sketch, "E306", {"start": v(-127.25, 381.85) * mm, "end": v(-127.25, 369.15) * mm});
            skLineSegment(sketch, "E307", {"start": v(127.25, 369.15) * mm, "end": v(127.25, 381.85) * mm});
            skLineSegment(sketch, "E308", {"start": v(-127.25, 381.85) * mm, "end": v(-180.6, 381.85) * mm});
            skLineSegment(sketch, "E309", {"start": v(-127.25, 369.15) * mm, "end": v(-180.6, 369.15) * mm});
            skLineSegment(sketch, "E310", {"start": v(127.25, 381.85) * mm, "end": v(180.6, 381.85) * mm});
            skLineSegment(sketch, "E311", {"start": v(127.25, 369.15) * mm, "end": v(180.6, 369.15) * mm});
            skLineSegment(sketch, "E312", {"start": v(-254, 283.65) * mm, "end": v(-76.2, 283.65) * mm});
            skLineSegment(sketch, "E313", {"start": v(-255.7, 277.3) * mm, "end": v(-76.2, 277.3) * mm});
            skLineSegment(sketch, "E314", {"start": v(254, 283.65) * mm, "end": v(76.2, 283.65) * mm});
            skLineSegment(sketch, "E315", {"start": v(255.7, 277.3) * mm, "end": v(76.2, 277.3) * mm});
            skLineSegment(sketch, "E316", {"start": v(266.7, 354.13) * mm, "end": v(266.7, 324.48) * mm});
            skArc(sketch, "E317", {"start": v(267.55, 415.07) * mm, "mid": v(266.92, 413.54) * mm, "end": v(266.7, 411.9) * mm});
            skArc(sketch, "E318", {"start": v(-266.7, 411.9) * mm, "mid": v(-266.92, 413.54) * mm, "end": v(-267.55, 415.07) * mm});
            skLineSegment(sketch, "E319", {"start": v(-266.7, 411.9) * mm, "end": v(266.7, 411.9) * mm});
            skLineSegment(sketch, "E320", {"start": v(267.55, 415.07) * mm, "end": v(-267.55, 415.07) * mm});
            skLineSegment(sketch, "E321", {"start": v(101.6, -424.6) * mm, "end": v(101.6, 261.2) * mm});
            skLineSegment(sketch, "E322", {"start": v(-101.6, -424.6) * mm, "end": v(-101.6, 261.2) * mm});
            skLineSegment(sketch, "E323", {"start": v(-76.2, -424.6) * mm, "end": v(-76.2, 261.2) * mm});
            skLineSegment(sketch, "E324", {"start": v(76.2, -424.6) * mm, "end": v(76.2, 261.2) * mm});
            skLineSegment(sketch, "E325", {"start": v(-76.2, 261.2) * mm, "end": v(50.8, 261.2) * mm});
            skLineSegment(sketch, "E326", {"start": v(50.8, 253.66) * mm, "end": v(76.2, 253.66) * mm});
            skLineSegment(sketch, "E327", {"start": v(-76.2, 253.66) * mm, "end": v(50.8, 253.66) * mm});
            skLineSegment(sketch, "E328", {"start": v(50.8, 246.11) * mm, "end": v(76.2, 246.11) * mm});
            skLineSegment(sketch, "E329", {"start": v(-76.2, 246.11) * mm, "end": v(50.8, 246.11) * mm});
            skLineSegment(sketch, "E330", {"start": v(50.8, 238.57) * mm, "end": v(76.2, 238.57) * mm});
            skLineSegment(sketch, "E331", {"start": v(-76.2, 238.57) * mm, "end": v(50.8, 238.57) * mm});
            skLineSegment(sketch, "E332", {"start": v(50.8, 231.03) * mm, "end": v(76.2, 231.03) * mm});
            skLineSegment(sketch, "E333", {"start": v(-76.2, 231.03) * mm, "end": v(50.8, 231.03) * mm});
            skLineSegment(sketch, "E334", {"start": v(50.8, 223.48) * mm, "end": v(76.2, 223.48) * mm});
            skLineSegment(sketch, "E335", {"start": v(-76.2, 223.48) * mm, "end": v(50.8, 223.48) * mm});
            skLineSegment(sketch, "E336", {"start": v(50.8, 215.94) * mm, "end": v(76.2, 215.94) * mm});
            skLineSegment(sketch, "E337", {"start": v(-76.2, 215.94) * mm, "end": v(50.8, 215.94) * mm});
            skLineSegment(sketch, "E338", {"start": v(50.8, 208.4) * mm, "end": v(76.2, 208.4) * mm});
            skLineSegment(sketch, "E339", {"start": v(-76.2, 208.4) * mm, "end": v(50.8, 208.4) * mm});
            skLineSegment(sketch, "E340", {"start": v(50.8, 200.85) * mm, "end": v(76.2, 200.85) * mm});
            skLineSegment(sketch, "E341", {"start": v(-76.2, 200.85) * mm, "end": v(50.8, 200.85) * mm});
            skLineSegment(sketch, "E342", {"start": v(50.8, 193.3) * mm, "end": v(76.2, 193.3) * mm});
            skLineSegment(sketch, "E343", {"start": v(-76.2, 193.3) * mm, "end": v(50.8, 193.3) * mm});
            skLineSegment(sketch, "E344", {"start": v(50.8, 185.76) * mm, "end": v(76.2, 185.76) * mm});
            skLineSegment(sketch, "E345", {"start": v(-76.2, 185.76) * mm, "end": v(50.8, 185.76) * mm});
            skLineSegment(sketch, "E346", {"start": v(50.8, 178.22) * mm, "end": v(76.2, 178.22) * mm});
            skLineSegment(sketch, "E347", {"start": v(-76.2, 178.22) * mm, "end": v(50.8, 178.22) * mm});
            skLineSegment(sketch, "E348", {"start": v(50.8, 170.68) * mm, "end": v(76.2, 170.68) * mm});
            skLineSegment(sketch, "E349", {"start": v(-76.2, 170.68) * mm, "end": v(50.8, 170.68) * mm});
            skLineSegment(sketch, "E350", {"start": v(50.8, 163.13) * mm, "end": v(76.2, 163.13) * mm});
            skLineSegment(sketch, "E351", {"start": v(-76.2, 163.13) * mm, "end": v(50.8, 163.13) * mm});
            skLineSegment(sketch, "E352", {"start": v(50.8, 155.59) * mm, "end": v(76.2, 155.59) * mm});
            skLineSegment(sketch, "E353", {"start": v(-76.2, 155.59) * mm, "end": v(50.8, 155.59) * mm});
            skLineSegment(sketch, "E354", {"start": v(50.8, 148.04) * mm, "end": v(76.2, 148.04) * mm});
            skLineSegment(sketch, "E355", {"start": v(-76.2, 148.04) * mm, "end": v(50.8, 148.04) * mm});
            skLineSegment(sketch, "E356", {"start": v(50.8, 140.5) * mm, "end": v(76.2, 140.5) * mm});
            skLineSegment(sketch, "E357", {"start": v(-76.2, 140.5) * mm, "end": v(50.8, 140.5) * mm});
            skLineSegment(sketch, "E358", {"start": v(50.8, 132.96) * mm, "end": v(76.2, 132.96) * mm});
            skLineSegment(sketch, "E359", {"start": v(-76.2, 132.96) * mm, "end": v(50.8, 132.96) * mm});
            skLineSegment(sketch, "E360", {"start": v(50.8, 125.41) * mm, "end": v(76.2, 125.41) * mm});
            skLineSegment(sketch, "E361", {"start": v(-76.2, 125.41) * mm, "end": v(50.8, 125.41) * mm});
            skLineSegment(sketch, "E362", {"start": v(50.8, 117.87) * mm, "end": v(76.2, 117.87) * mm});
            skLineSegment(sketch, "E363", {"start": v(-76.2, 117.87) * mm, "end": v(50.8, 117.87) * mm});
            skLineSegment(sketch, "E364", {"start": v(50.8, 110.32) * mm, "end": v(76.2, 110.32) * mm});
            skLineSegment(sketch, "E365", {"start": v(-76.2, 110.32) * mm, "end": v(50.8, 110.32) * mm});
            skLineSegment(sketch, "E366", {"start": v(50.8, 102.78) * mm, "end": v(76.2, 102.78) * mm});
            skLineSegment(sketch, "E367", {"start": v(-76.2, 102.78) * mm, "end": v(50.8, 102.78) * mm});
            skLineSegment(sketch, "E368", {"start": v(50.8, 95.24) * mm, "end": v(76.2, 95.24) * mm});
            skLineSegment(sketch, "E369", {"start": v(-76.2, 95.24) * mm, "end": v(50.8, 95.24) * mm});
            skLineSegment(sketch, "E370", {"start": v(50.8, 87.7) * mm, "end": v(76.2, 87.7) * mm});
            skLineSegment(sketch, "E371", {"start": v(-76.2, 87.7) * mm, "end": v(50.8, 87.7) * mm});
            skLineSegment(sketch, "E372", {"start": v(50.8, 80.15) * mm, "end": v(76.2, 80.15) * mm});
            skLineSegment(sketch, "E373", {"start": v(-76.2, 80.15) * mm, "end": v(50.8, 80.15) * mm});
            skLineSegment(sketch, "E374", {"start": v(50.8, 72.6) * mm, "end": v(76.2, 72.6) * mm});
            skLineSegment(sketch, "E375", {"start": v(-76.2, 72.6) * mm, "end": v(50.8, 72.6) * mm});
            skLineSegment(sketch, "E376", {"start": v(50.8, 65.06) * mm, "end": v(76.2, 65.06) * mm});
            skLineSegment(sketch, "E377", {"start": v(-76.2, 65.06) * mm, "end": v(50.8, 65.06) * mm});
            skLineSegment(sketch, "E378", {"start": v(50.8, 57.52) * mm, "end": v(76.2, 57.52) * mm});
            skLineSegment(sketch, "E379", {"start": v(-76.2, 57.52) * mm, "end": v(50.8, 57.52) * mm});
            skLineSegment(sketch, "E380", {"start": v(50.8, 49.97) * mm, "end": v(76.2, 49.97) * mm});
            skLineSegment(sketch, "E381", {"start": v(-76.2, 49.97) * mm, "end": v(50.8, 49.97) * mm});
            skLineSegment(sketch, "E382", {"start": v(50.8, 42.43) * mm, "end": v(76.2, 42.43) * mm});
            skLineSegment(sketch, "E383", {"start": v(-76.2, 42.43) * mm, "end": v(50.8, 42.43) * mm});
            skLineSegment(sketch, "E384", {"start": v(50.8, 34.89) * mm, "end": v(76.2, 34.89) * mm});
            skLineSegment(sketch, "E385", {"start": v(-76.2, 34.89) * mm, "end": v(50.8, 34.89) * mm});
            skLineSegment(sketch, "E386", {"start": v(50.8, 27.34) * mm, "end": v(76.2, 27.34) * mm});
            skLineSegment(sketch, "E387", {"start": v(-76.2, 27.34) * mm, "end": v(50.8, 27.34) * mm});
            skLineSegment(sketch, "E388", {"start": v(50.8, 19.8) * mm, "end": v(76.2, 19.8) * mm});
            skLineSegment(sketch, "E389", {"start": v(-76.2, 19.8) * mm, "end": v(50.8, 19.8) * mm});
            skLineSegment(sketch, "E390", {"start": v(50.8, 12.26) * mm, "end": v(76.2, 12.26) * mm});
            skLineSegment(sketch, "E391", {"start": v(-76.2, 12.26) * mm, "end": v(50.8, 12.26) * mm});
            skLineSegment(sketch, "E392", {"start": v(50.8, 4.71) * mm, "end": v(76.2, 4.71) * mm});
            skLineSegment(sketch, "E393", {"start": v(-76.2, 4.71) * mm, "end": v(50.8, 4.71) * mm});
            skLineSegment(sketch, "E394", {"start": v(50.8, -2.83) * mm, "end": v(76.2, -2.83) * mm});
            skLineSegment(sketch, "E395", {"start": v(-76.2, -2.83) * mm, "end": v(50.8, -2.83) * mm});
            skLineSegment(sketch, "E396", {"start": v(50.8, -10.38) * mm, "end": v(76.2, -10.38) * mm});
            skLineSegment(sketch, "E397", {"start": v(-76.2, -10.38) * mm, "end": v(50.8, -10.38) * mm});
            skLineSegment(sketch, "E398", {"start": v(50.8, -17.92) * mm, "end": v(76.2, -17.92) * mm});
            skLineSegment(sketch, "E399", {"start": v(-76.2, -17.92) * mm, "end": v(50.8, -17.92) * mm});
            skLineSegment(sketch, "E400", {"start": v(50.8, -25.46) * mm, "end": v(76.2, -25.46) * mm});
            skLineSegment(sketch, "E401", {"start": v(-76.2, -25.46) * mm, "end": v(50.8, -25.46) * mm});
            skLineSegment(sketch, "E402", {"start": v(50.8, -33) * mm, "end": v(76.2, -33) * mm});
            skLineSegment(sketch, "E403", {"start": v(-76.2, -33) * mm, "end": v(50.8, -33) * mm});
            skLineSegment(sketch, "E404", {"start": v(50.8, -40.55) * mm, "end": v(76.2, -40.55) * mm});
            skLineSegment(sketch, "E405", {"start": v(-76.2, -40.55) * mm, "end": v(50.8, -40.55) * mm});
            skLineSegment(sketch, "E406", {"start": v(50.8, -48.1) * mm, "end": v(76.2, -48.1) * mm});
            skLineSegment(sketch, "E407", {"start": v(-76.2, -48.1) * mm, "end": v(50.8, -48.1) * mm});
            skLineSegment(sketch, "E408", {"start": v(50.8, -55.64) * mm, "end": v(76.2, -55.64) * mm});
            skLineSegment(sketch, "E409", {"start": v(-76.2, -55.64) * mm, "end": v(50.8, -55.64) * mm});
            skLineSegment(sketch, "E410", {"start": v(50.8, -63.18) * mm, "end": v(76.2, -63.18) * mm});
            skLineSegment(sketch, "E411", {"start": v(-76.2, -63.18) * mm, "end": v(50.8, -63.18) * mm});
            skLineSegment(sketch, "E412", {"start": v(50.8, -70.73) * mm, "end": v(76.2, -70.73) * mm});
            skLineSegment(sketch, "E413", {"start": v(-76.2, -70.73) * mm, "end": v(50.8, -70.73) * mm});
            skLineSegment(sketch, "E414", {"start": v(50.8, -78.27) * mm, "end": v(76.2, -78.27) * mm});
            skLineSegment(sketch, "E415", {"start": v(-76.2, -78.27) * mm, "end": v(50.8, -78.27) * mm});
            skLineSegment(sketch, "E416", {"start": v(50.8, -85.81) * mm, "end": v(76.2, -85.81) * mm});
            skLineSegment(sketch, "E417", {"start": v(-76.2, -85.81) * mm, "end": v(50.8, -85.81) * mm});
            skLineSegment(sketch, "E418", {"start": v(50.8, -93.36) * mm, "end": v(76.2, -93.36) * mm});
            skLineSegment(sketch, "E419", {"start": v(-76.2, -93.36) * mm, "end": v(50.8, -93.36) * mm});
            skLineSegment(sketch, "E420", {"start": v(50.8, -100.9) * mm, "end": v(76.2, -100.9) * mm});
            skLineSegment(sketch, "E421", {"start": v(-76.2, -100.9) * mm, "end": v(50.8, -100.9) * mm});
            skLineSegment(sketch, "E422", {"start": v(50.8, -108.45) * mm, "end": v(76.2, -108.45) * mm});
            skLineSegment(sketch, "E423", {"start": v(-76.2, -108.45) * mm, "end": v(50.8, -108.45) * mm});
            skLineSegment(sketch, "E424", {"start": v(50.8, -115.99) * mm, "end": v(76.2, -115.99) * mm});
            skLineSegment(sketch, "E425", {"start": v(-76.2, -115.99) * mm, "end": v(50.8, -115.99) * mm});
            skLineSegment(sketch, "E426", {"start": v(50.8, -123.53) * mm, "end": v(76.2, -123.53) * mm});
            skLineSegment(sketch, "E427", {"start": v(-76.2, -123.53) * mm, "end": v(50.8, -123.53) * mm});
            skLineSegment(sketch, "E428", {"start": v(50.8, -131.08) * mm, "end": v(76.2, -131.08) * mm});
            skLineSegment(sketch, "E429", {"start": v(-76.2, -131.08) * mm, "end": v(50.8, -131.08) * mm});
            skLineSegment(sketch, "E430", {"start": v(50.8, -138.62) * mm, "end": v(76.2, -138.62) * mm});
            skLineSegment(sketch, "E431", {"start": v(-76.2, -138.62) * mm, "end": v(50.8, -138.62) * mm});
            skLineSegment(sketch, "E432", {"start": v(50.8, -146.16) * mm, "end": v(76.2, -146.16) * mm});
            skLineSegment(sketch, "E433", {"start": v(-76.2, -146.16) * mm, "end": v(50.8, -146.16) * mm});
            skLineSegment(sketch, "E434", {"start": v(50.8, -153.7) * mm, "end": v(76.2, -153.7) * mm});
            skLineSegment(sketch, "E435", {"start": v(-76.2, -153.7) * mm, "end": v(50.8, -153.7) * mm});
            skLineSegment(sketch, "E436", {"start": v(50.8, -161.25) * mm, "end": v(76.2, -161.25) * mm});
            skLineSegment(sketch, "E437", {"start": v(-76.2, -161.25) * mm, "end": v(50.8, -161.25) * mm});
            skLineSegment(sketch, "E438", {"start": v(50.8, -168.8) * mm, "end": v(76.2, -168.8) * mm});
            skLineSegment(sketch, "E439", {"start": v(-76.2, -168.8) * mm, "end": v(50.8, -168.8) * mm});
            skLineSegment(sketch, "E440", {"start": v(50.8, -176.34) * mm, "end": v(76.2, -176.34) * mm});
            skLineSegment(sketch, "E441", {"start": v(-76.2, -176.34) * mm, "end": v(50.8, -176.34) * mm});
            skLineSegment(sketch, "E442", {"start": v(50.8, -183.88) * mm, "end": v(76.2, -183.88) * mm});
            skLineSegment(sketch, "E443", {"start": v(-76.2, -183.88) * mm, "end": v(50.8, -183.88) * mm});
            skLineSegment(sketch, "E444", {"start": v(50.8, -191.43) * mm, "end": v(76.2, -191.43) * mm});
            skLineSegment(sketch, "E445", {"start": v(-76.2, -191.43) * mm, "end": v(50.8, -191.43) * mm});
            skLineSegment(sketch, "E446", {"start": v(50.8, -198.97) * mm, "end": v(76.2, -198.97) * mm});
            skLineSegment(sketch, "E447", {"start": v(-76.2, -198.97) * mm, "end": v(50.8, -198.97) * mm});
            skLineSegment(sketch, "E448", {"start": v(50.8, -206.51) * mm, "end": v(76.2, -206.51) * mm});
            skLineSegment(sketch, "E449", {"start": v(-76.2, -206.51) * mm, "end": v(50.8, -206.51) * mm});
            skLineSegment(sketch, "E450", {"start": v(50.8, -214.06) * mm, "end": v(76.2, -214.06) * mm});
            skLineSegment(sketch, "E451", {"start": v(-76.2, -214.06) * mm, "end": v(50.8, -214.06) * mm});
            skLineSegment(sketch, "E452", {"start": v(50.8, -221.6) * mm, "end": v(76.2, -221.6) * mm});
            skLineSegment(sketch, "E453", {"start": v(-76.2, -221.6) * mm, "end": v(50.8, -221.6) * mm});
            skLineSegment(sketch, "E454", {"start": v(50.8, -229.15) * mm, "end": v(76.2, -229.15) * mm});
            skLineSegment(sketch, "E455", {"start": v(-76.2, -229.15) * mm, "end": v(50.8, -229.15) * mm});
            skLineSegment(sketch, "E456", {"start": v(50.8, -236.7) * mm, "end": v(76.2, -236.7) * mm});
            skLineSegment(sketch, "E457", {"start": v(-76.2, -236.7) * mm, "end": v(50.8, -236.7) * mm});
            skLineSegment(sketch, "E458", {"start": v(50.8, -244.23) * mm, "end": v(76.2, -244.23) * mm});
            skLineSegment(sketch, "E459", {"start": v(-76.2, -244.23) * mm, "end": v(50.8, -244.23) * mm});
            skLineSegment(sketch, "E460", {"start": v(50.8, -251.78) * mm, "end": v(76.2, -251.78) * mm});
            skLineSegment(sketch, "E461", {"start": v(-76.2, -251.78) * mm, "end": v(50.8, -251.78) * mm});
            skLineSegment(sketch, "E462", {"start": v(50.8, -259.32) * mm, "end": v(76.2, -259.32) * mm});
            skLineSegment(sketch, "E463", {"start": v(-76.2, -259.32) * mm, "end": v(50.8, -259.32) * mm});
            skLineSegment(sketch, "E464", {"start": v(50.8, -266.87) * mm, "end": v(76.2, -266.87) * mm});
            skLineSegment(sketch, "E465", {"start": v(-76.2, -266.87) * mm, "end": v(50.8, -266.87) * mm});
            skLineSegment(sketch, "E466", {"start": v(50.8, -274.4) * mm, "end": v(76.2, -274.4) * mm});
            skLineSegment(sketch, "E467", {"start": v(-76.2, -274.4) * mm, "end": v(50.8, -274.4) * mm});
            skLineSegment(sketch, "E468", {"start": v(50.8, -281.95) * mm, "end": v(76.2, -281.95) * mm});
            skLineSegment(sketch, "E469", {"start": v(-76.2, -281.95) * mm, "end": v(50.8, -281.95) * mm});
            skLineSegment(sketch, "E470", {"start": v(50.8, -289.5) * mm, "end": v(76.2, -289.5) * mm});
            skLineSegment(sketch, "E471", {"start": v(-76.2, -289.5) * mm, "end": v(50.8, -289.5) * mm});
            skLineSegment(sketch, "E472", {"start": v(50.8, -297.04) * mm, "end": v(76.2, -297.04) * mm});
            skLineSegment(sketch, "E473", {"start": v(-76.2, -297.04) * mm, "end": v(50.8, -297.04) * mm});
            skLineSegment(sketch, "E474", {"start": v(50.8, -304.58) * mm, "end": v(76.2, -304.58) * mm});
            skLineSegment(sketch, "E475", {"start": v(-76.2, -304.58) * mm, "end": v(50.8, -304.58) * mm});
            skLineSegment(sketch, "E476", {"start": v(50.8, -312.13) * mm, "end": v(76.2, -312.13) * mm});
            skLineSegment(sketch, "E477", {"start": v(-76.2, -312.13) * mm, "end": v(50.8, -312.13) * mm});
            skLineSegment(sketch, "E478", {"start": v(50.8, -319.67) * mm, "end": v(76.2, -319.67) * mm});
            skLineSegment(sketch, "E479", {"start": v(-76.2, -319.67) * mm, "end": v(50.8, -319.67) * mm});
            skLineSegment(sketch, "E480", {"start": v(50.8, -327.22) * mm, "end": v(76.2, -327.22) * mm});
            skLineSegment(sketch, "E481", {"start": v(-76.2, -327.22) * mm, "end": v(50.8, -327.22) * mm});
            skLineSegment(sketch, "E482", {"start": v(50.8, -334.76) * mm, "end": v(76.2, -334.76) * mm});
            skLineSegment(sketch, "E483", {"start": v(-76.2, -334.76) * mm, "end": v(50.8, -334.76) * mm});
            skLineSegment(sketch, "E484", {"start": v(50.8, -342.3) * mm, "end": v(76.2, -342.3) * mm});
            skLineSegment(sketch, "E485", {"start": v(-76.2, -342.3) * mm, "end": v(50.8, -342.3) * mm});
            skLineSegment(sketch, "E486", {"start": v(50.8, -349.85) * mm, "end": v(76.2, -349.85) * mm});
            skLineSegment(sketch, "E487", {"start": v(-76.2, -349.85) * mm, "end": v(50.8, -349.85) * mm});
            skLineSegment(sketch, "E488", {"start": v(50.8, -357.4) * mm, "end": v(76.2, -357.4) * mm});
            skLineSegment(sketch, "E489", {"start": v(-76.2, -357.4) * mm, "end": v(50.8, -357.4) * mm});
            skLineSegment(sketch, "E490", {"start": v(50.8, -364.93) * mm, "end": v(76.2, -364.93) * mm});
            skLineSegment(sketch, "E491", {"start": v(-76.2, -364.93) * mm, "end": v(50.8, -364.93) * mm});
            skLineSegment(sketch, "E492", {"start": v(50.8, -372.48) * mm, "end": v(76.2, -372.48) * mm});
            skLineSegment(sketch, "E493", {"start": v(-76.2, -372.48) * mm, "end": v(50.8, -372.48) * mm});
            skLineSegment(sketch, "E494", {"start": v(50.8, -380.02) * mm, "end": v(76.2, -380.02) * mm});
            skLineSegment(sketch, "E495", {"start": v(-76.2, -380.02) * mm, "end": v(50.8, -380.02) * mm});
            skLineSegment(sketch, "E496", {"start": v(50.8, -387.57) * mm, "end": v(76.2, -387.57) * mm});
            skLineSegment(sketch, "E497", {"start": v(-76.2, -387.57) * mm, "end": v(50.8, -387.57) * mm});
            skLineSegment(sketch, "E498", {"start": v(50.8, -395.1) * mm, "end": v(76.2, -395.1) * mm});
            skLineSegment(sketch, "E499", {"start": v(-76.2, -395.1) * mm, "end": v(50.8, -395.1) * mm});
            skLineSegment(sketch, "E500", {"start": v(50.8, -402.65) * mm, "end": v(76.2, -402.65) * mm});
            skLineSegment(sketch, "E501", {"start": v(-76.2, -402.65) * mm, "end": v(50.8, -402.65) * mm});
            skLineSegment(sketch, "E502", {"start": v(50.8, -410.2) * mm, "end": v(76.2, -410.2) * mm});
            skLineSegment(sketch, "E503", {"start": v(-76.2, -410.2) * mm, "end": v(50.8, -410.2) * mm});
            skLineSegment(sketch, "E504", {"start": v(50.8, -417.74) * mm, "end": v(76.2, -417.74) * mm});
            skLineSegment(sketch, "E505", {"start": v(-76.2, -417.74) * mm, "end": v(50.8, -417.74) * mm});
            skLineSegment(sketch, "E506", {"start": v(76.2, -424.6) * mm, "end": v(1003.85, -424.6) * mm});
            skLineSegment(sketch, "E507", {"start": v(1003.85, -424.6) * mm, "end": v(1156.25, -424.6) * mm});
            skLineSegment(sketch, "E508", {"start": v(1156.25, -424.6) * mm, "end": v(303.1, 261.2) * mm});
            skLineSegment(sketch, "E509", {"start": v(-1003.85, -424.6) * mm, "end": v(-1156.25, -424.6) * mm});
            skLineSegment(sketch, "E510", {"start": v(-1156.25, -424.6) * mm, "end": v(-303.1, 261.2) * mm});
            skSolve(sketch);
        }
        {
            var Q0;
            Q0=qCreatedBy(makeId("Right.planeOp"),FACE);
            var sketch = newSketch(context, id + "F1", { "sketchPlane" : qUnion([Q0])});
            skLineSegment(sketch, "E511", {"start": v(-254, 387.76) * mm, "end": v(-254, 363.24) * mm});
            skLineSegment(sketch, "E512", {"start": v(-265, 261.2) * mm, "end": v(265, 261.2) * mm});
            skLineSegment(sketch, "E513", {"start": v(254, 283.65) * mm, "end": v(254, 324.48) * mm});
            skLineSegment(sketch, "E514", {"start": v(-266.7, 337.4) * mm, "end": v(266.7, 337.4) * mm});
            skLineSegment(sketch, "E515", {"start": v(-266.7, 363.24) * mm, "end": v(266.7, 363.24) * mm});
            skLineSegment(sketch, "E516", {"start": v(-266.7, 354.13) * mm, "end": v(-266.7, 363.24) * mm});
            skLineSegment(sketch, "E517", {"start": v(-266.7, 350.32) * mm, "end": v(266.7, 350.32) * mm});
            skLineSegment(sketch, "E518", {"start": v(-254, 324.48) * mm, "end": v(-254, 283.65) * mm});
            skLineSegment(sketch, "E519", {"start": v(254, 363.24) * mm, "end": v(254, 387.76) * mm});
            skLineSegment(sketch, "E520", {"start": v(-266.7, 387.76) * mm, "end": v(266.7, 387.76) * mm});
            skLineSegment(sketch, "E521", {"start": v(-266.7, 387.76) * mm, "end": v(-266.7, 404.49) * mm});
            skLineSegment(sketch, "E522", {"start": v(266.7, 387.76) * mm, "end": v(266.7, 404.49) * mm});
            skLineSegment(sketch, "E523", {"start": v(-266.7, 400.68) * mm, "end": v(266.7, 400.68) * mm});
            skLineSegment(sketch, "E524", {"start": v(266.7, 404.49) * mm, "end": v(266.7, 411.9) * mm});
            skLineSegment(sketch, "E525", {"start": v(-266.7, 404.49) * mm, "end": v(-266.7, 411.9) * mm});
            skLineSegment(sketch, "E526", {"start": v(266.7, 354.13) * mm, "end": v(266.7, 363.24) * mm});
            skLineSegment(sketch, "E527", {"start": v(-255.7, 277.3) * mm, "end": v(-265, 261.2) * mm});
            skLineSegment(sketch, "E528", {"start": v(255.7, 277.3) * mm, "end": v(265, 261.2) * mm});
            skArc(sketch, "E529", {"start": v(-255.7, 277.3) * mm, "mid": v(-254.43, 280.37) * mm, "end": v(-254, 283.65) * mm});
            skArc(sketch, "E530", {"start": v(254, 283.65) * mm, "mid": v(254.43, 280.37) * mm, "end": v(255.7, 277.3) * mm});
            skLineSegment(sketch, "E531", {"start": v(0, 312) * mm, "end": v(76.2, 312) * mm});
            skLineSegment(sketch, "E532", {"start": v(76.2, 312) * mm, "end": v(76.2, 261.2) * mm});
            skLineSegment(sketch, "E533", {"start": v(0, 312) * mm, "end": v(-76.2, 312) * mm});
            skLineSegment(sketch, "E534", {"start": v(-76.2, 312) * mm, "end": v(-76.2, 261.2) * mm});
            skLineSegment(sketch, "E535", {"start": v(-38.1, 305.65) * mm, "end": v(-38.1, 261.2) * mm});
            skLineSegment(sketch, "E536", {"start": v(38.1, 305.65) * mm, "end": v(38.1, 261.2) * mm});
            skLineSegment(sketch, "E537", {"start": v(50.8, 305.65) * mm, "end": v(50.8, 261.2) * mm});
            skLineSegment(sketch, "E538", {"start": v(-50.8, 305.65) * mm, "end": v(-50.8, 261.2) * mm});
            skLineSegment(sketch, "E539", {"start": v(-303.1, 261.2) * mm, "end": v(-265, 261.2) * mm});
            skLineSegment(sketch, "E540", {"start": v(303.1, 261.2) * mm, "end": v(265, 261.2) * mm});
            skLineSegment(sketch, "E541", {"start": v(-549.38, 32.6) * mm, "end": v(-101.6, 32.6) * mm});
            skLineSegment(sketch, "E542", {"start": v(-631.47, -43.6) * mm, "end": v(-101.6, -43.6) * mm});
            skLineSegment(sketch, "E543", {"start": v(-303.1, 261.2) * mm, "end": v(-347.1, 185) * mm});
            skLineSegment(sketch, "E544", {"start": v(-385.2, 185) * mm, "end": v(-429.19, 108.8) * mm});
            skLineSegment(sketch, "E545", {"start": v(-467.29, 108.8) * mm, "end": v(-511.28, 32.6) * mm});
            skLineSegment(sketch, "E546", {"start": v(-549.38, 32.6) * mm, "end": v(-593.37, -43.6) * mm});
            skLineSegment(sketch, "E547", {"start": v(-631.47, -43.6) * mm, "end": v(-675.47, -119.8) * mm});
            skLineSegment(sketch, "E548", {"start": v(-713.57, -119.8) * mm, "end": v(-757.56, -196) * mm});
            skLineSegment(sketch, "E549", {"start": v(-795.66, -196) * mm, "end": v(-839.66, -272.2) * mm});
            skLineSegment(sketch, "E550", {"start": v(-877.76, -272.2) * mm, "end": v(-921.75, -348.4) * mm});
            skLineSegment(sketch, "E551", {"start": v(-959.85, -348.4) * mm, "end": v(-1003.85, -424.6) * mm});
            skLineSegment(sketch, "E552", {"start": v(303.1, 261.2) * mm, "end": v(347.1, 185) * mm});
            skLineSegment(sketch, "E553", {"start": v(385.2, 185) * mm, "end": v(429.19, 108.8) * mm});
            skLineSegment(sketch, "E554", {"start": v(467.29, 108.8) * mm, "end": v(511.28, 32.6) * mm});
            skLineSegment(sketch, "E555", {"start": v(549.38, 32.6) * mm, "end": v(593.37, -43.6) * mm});
            skLineSegment(sketch, "E556", {"start": v(631.47, -43.6) * mm, "end": v(675.47, -119.8) * mm});
            skLineSegment(sketch, "E557", {"start": v(713.57, -119.8) * mm, "end": v(757.56, -196) * mm});
            skLineSegment(sketch, "E558", {"start": v(795.66, -196) * mm, "end": v(839.66, -272.2) * mm});
            skLineSegment(sketch, "E559", {"start": v(877.76, -272.2) * mm, "end": v(921.75, -348.4) * mm});
            skLineSegment(sketch, "E560", {"start": v(959.85, -348.4) * mm, "end": v(1003.85, -424.6) * mm});
            skLineSegment(sketch, "E561", {"start": v(-959.85, -348.4) * mm, "end": v(-101.6, -348.4) * mm});
            skLineSegment(sketch, "E562", {"start": v(-795.66, -196) * mm, "end": v(-101.6, -196) * mm});
            skLineSegment(sketch, "E563", {"start": v(-877.76, -272.2) * mm, "end": v(-101.6, -272.2) * mm});
            skLineSegment(sketch, "E564", {"start": v(-713.57, -119.8) * mm, "end": v(-101.6, -119.8) * mm});
            skLineSegment(sketch, "E565", {"start": v(-385.2, 185) * mm, "end": v(-101.6, 185) * mm});
            skLineSegment(sketch, "E566", {"start": v(-467.29, 108.8) * mm, "end": v(-101.6, 108.8) * mm});
            skLineSegment(sketch, "E567", {"start": v(-870, -399.2) * mm, "end": v(-870, -361.1) * mm});
            skLineSegment(sketch, "E568", {"start": v(-736.15, -399.2) * mm, "end": v(-736.15, -361.1) * mm});
            skLineSegment(sketch, "E569", {"start": v(-602.3, -399.2) * mm, "end": v(-602.3, -361.1) * mm});
            skLineSegment(sketch, "E570", {"start": v(-870, -361.1) * mm, "end": v(-736.15, -361.1) * mm});
            skLineSegment(sketch, "E571", {"start": v(-989.18, -399.2) * mm, "end": v(-870, -399.2) * mm});
            skLineSegment(sketch, "E572", {"start": v(-736.15, -399.2) * mm, "end": v(-602.3, -399.2) * mm});
            skLineSegment(sketch, "E573", {"start": v(-602.3, -361.1) * mm, "end": v(-468.46, -361.1) * mm});
            skLineSegment(sketch, "E574", {"start": v(-468.46, -399.2) * mm, "end": v(-334.62, -399.2) * mm});
            skLineSegment(sketch, "E575", {"start": v(-334.62, -361.1) * mm, "end": v(-200.77, -361.1) * mm});
            skLineSegment(sketch, "E576", {"start": v(101.6, -399.2) * mm, "end": v(200.77, -399.2) * mm});
            skLineSegment(sketch, "E577", {"start": v(200.77, -361.1) * mm, "end": v(334.62, -361.1) * mm});
            skLineSegment(sketch, "E578", {"start": v(870, -399.2) * mm, "end": v(989.18, -399.2) * mm});
            skLineSegment(sketch, "E579", {"start": v(736.15, -361.1) * mm, "end": v(870, -361.1) * mm});
            skLineSegment(sketch, "E580", {"start": v(602.3, -399.2) * mm, "end": v(736.15, -399.2) * mm});
            skLineSegment(sketch, "E581", {"start": v(468.46, -361.1) * mm, "end": v(602.3, -361.1) * mm});
            skLineSegment(sketch, "E582", {"start": v(-1003.85, -424.6) * mm, "end": v(76.2, -424.6) * mm});
            skLineSegment(sketch, "E583", {"start": v(-468.46, -399.2) * mm, "end": v(-468.46, -361.1) * mm});
            skLineSegment(sketch, "E584", {"start": v(-334.62, -399.2) * mm, "end": v(-334.62, -361.1) * mm});
            skLineSegment(sketch, "E585", {"start": v(-200.77, -399.2) * mm, "end": v(-200.77, -361.1) * mm});
            skLineSegment(sketch, "E586", {"start": v(-200.77, -399.2) * mm, "end": v(-101.6, -399.2) * mm});
            skLineSegment(sketch, "E587", {"start": v(200.77, -399.2) * mm, "end": v(200.77, -361.1) * mm});
            skLineSegment(sketch, "E588", {"start": v(334.62, -399.2) * mm, "end": v(468.46, -399.2) * mm});
            skLineSegment(sketch, "E589", {"start": v(334.62, -399.2) * mm, "end": v(334.62, -361.1) * mm});
            skLineSegment(sketch, "E590", {"start": v(468.46, -399.2) * mm, "end": v(468.46, -361.1) * mm});
            skLineSegment(sketch, "E591", {"start": v(602.3, -399.2) * mm, "end": v(602.3, -361.1) * mm});
            skLineSegment(sketch, "E592", {"start": v(736.15, -399.2) * mm, "end": v(736.15, -361.1) * mm});
            skLineSegment(sketch, "E593", {"start": v(870, -361.1) * mm, "end": v(870, -399.2) * mm});
            skLineSegment(sketch, "E594", {"start": v(101.6, -348.4) * mm, "end": v(959.85, -348.4) * mm});
            skLineSegment(sketch, "E595", {"start": v(101.6, -272.2) * mm, "end": v(877.76, -272.2) * mm});
            skLineSegment(sketch, "E596", {"start": v(101.6, -196) * mm, "end": v(795.66, -196) * mm});
            skLineSegment(sketch, "E597", {"start": v(101.6, -119.8) * mm, "end": v(713.57, -119.8) * mm});
            skLineSegment(sketch, "E598", {"start": v(101.6, -43.6) * mm, "end": v(631.47, -43.6) * mm});
            skLineSegment(sketch, "E599", {"start": v(101.6, 32.6) * mm, "end": v(549.38, 32.6) * mm});
            skLineSegment(sketch, "E600", {"start": v(101.6, 108.8) * mm, "end": v(467.29, 108.8) * mm});
            skLineSegment(sketch, "E601", {"start": v(101.6, 185) * mm, "end": v(385.2, 185) * mm});
            skLineSegment(sketch, "E602", {"start": v(-292.38, 248.5) * mm, "end": v(-247.41, 248.5) * mm});
            skLineSegment(sketch, "E603", {"start": v(-202.44, 248.5) * mm, "end": v(-157.47, 248.5) * mm});
            skLineSegment(sketch, "E604", {"start": v(-112.5, 248.5) * mm, "end": v(-101.6, 248.5) * mm});
            skLineSegment(sketch, "E605", {"start": v(101.6, 248.5) * mm, "end": v(112.37, 248.5) * mm});
            skLineSegment(sketch, "E606", {"start": v(157.34, 248.5) * mm, "end": v(202.31, 248.5) * mm});
            skLineSegment(sketch, "E607", {"start": v(247.28, 248.5) * mm, "end": v(292.26, 248.5) * mm});
            skLineSegment(sketch, "E608", {"start": v(-292.38, 210.4) * mm, "end": v(-292.38, 248.5) * mm});
            skLineSegment(sketch, "E609", {"start": v(-247.41, 210.4) * mm, "end": v(-247.41, 248.5) * mm});
            skLineSegment(sketch, "E610", {"start": v(-202.44, 210.4) * mm, "end": v(-202.44, 248.5) * mm});
            skLineSegment(sketch, "E611", {"start": v(-157.47, 210.4) * mm, "end": v(-157.47, 248.5) * mm});
            skLineSegment(sketch, "E612", {"start": v(-112.5, 210.4) * mm, "end": v(-112.5, 248.5) * mm});
            skLineSegment(sketch, "E613", {"start": v(112.37, 210.4) * mm, "end": v(112.37, 248.5) * mm});
            skLineSegment(sketch, "E614", {"start": v(157.34, 210.4) * mm, "end": v(157.34, 248.5) * mm});
            skLineSegment(sketch, "E615", {"start": v(202.31, 210.4) * mm, "end": v(202.31, 248.5) * mm});
            skLineSegment(sketch, "E616", {"start": v(247.28, 210.4) * mm, "end": v(247.28, 248.5) * mm});
            skLineSegment(sketch, "E617", {"start": v(-332.43, 210.4) * mm, "end": v(-292.38, 210.4) * mm});
            skLineSegment(sketch, "E618", {"start": v(-247.41, 210.4) * mm, "end": v(-202.44, 210.4) * mm});
            skLineSegment(sketch, "E619", {"start": v(-157.47, 210.4) * mm, "end": v(-112.5, 210.4) * mm});
            skLineSegment(sketch, "E620", {"start": v(202.31, 210.4) * mm, "end": v(247.28, 210.4) * mm});
            skLineSegment(sketch, "E621", {"start": v(292.26, 210.4) * mm, "end": v(332.3, 210.4) * mm});
            skLineSegment(sketch, "E622", {"start": v(112.37, 210.4) * mm, "end": v(157.34, 210.4) * mm});
            skLineSegment(sketch, "E623", {"start": v(292.26, 248.5) * mm, "end": v(292.26, 210.4) * mm});
            skLineSegment(sketch, "E624", {"start": v(-364.59, 172.3) * mm, "end": v(-308.5, 172.3) * mm});
            skLineSegment(sketch, "E625", {"start": v(-252.42, 172.3) * mm, "end": v(-196.34, 172.3) * mm});
            skLineSegment(sketch, "E626", {"start": v(-140.26, 172.3) * mm, "end": v(-101.6, 172.3) * mm});
            skLineSegment(sketch, "E627", {"start": v(101.6, 172.3) * mm, "end": v(140.15, 172.3) * mm});
            skLineSegment(sketch, "E628", {"start": v(196.23, 172.3) * mm, "end": v(252.31, 172.3) * mm});
            skLineSegment(sketch, "E629", {"start": v(308.4, 172.3) * mm, "end": v(364.47, 172.3) * mm});
            skLineSegment(sketch, "E630", {"start": v(-364.59, 134.2) * mm, "end": v(-364.59, 172.3) * mm});
            skLineSegment(sketch, "E631", {"start": v(-308.5, 134.2) * mm, "end": v(-308.5, 172.3) * mm});
            skLineSegment(sketch, "E632", {"start": v(-252.42, 134.2) * mm, "end": v(-252.42, 172.3) * mm});
            skLineSegment(sketch, "E633", {"start": v(-196.34, 134.2) * mm, "end": v(-196.34, 172.3) * mm});
            skLineSegment(sketch, "E634", {"start": v(-140.26, 134.2) * mm, "end": v(-140.26, 172.3) * mm});
            skLineSegment(sketch, "E635", {"start": v(140.15, 134.2) * mm, "end": v(140.15, 172.3) * mm});
            skLineSegment(sketch, "E636", {"start": v(196.23, 134.2) * mm, "end": v(196.23, 172.3) * mm});
            skLineSegment(sketch, "E637", {"start": v(252.31, 134.2) * mm, "end": v(252.31, 172.3) * mm});
            skLineSegment(sketch, "E638", {"start": v(308.4, 134.2) * mm, "end": v(308.4, 172.3) * mm});
            skLineSegment(sketch, "E639", {"start": v(-414.52, 134.2) * mm, "end": v(-364.59, 134.2) * mm});
            skLineSegment(sketch, "E640", {"start": v(-308.5, 134.2) * mm, "end": v(-252.42, 134.2) * mm});
            skLineSegment(sketch, "E641", {"start": v(-196.34, 134.2) * mm, "end": v(-140.26, 134.2) * mm});
            skLineSegment(sketch, "E642", {"start": v(252.31, 134.2) * mm, "end": v(308.4, 134.2) * mm});
            skLineSegment(sketch, "E643", {"start": v(364.47, 134.2) * mm, "end": v(414.41, 134.2) * mm});
            skLineSegment(sketch, "E644", {"start": v(140.15, 134.2) * mm, "end": v(196.23, 134.2) * mm});
            skLineSegment(sketch, "E645", {"start": v(364.47, 172.3) * mm, "end": v(364.47, 134.2) * mm});
            skLineSegment(sketch, "E646", {"start": v(-436.79, 96.1) * mm, "end": v(-369.6, 96.1) * mm});
            skLineSegment(sketch, "E647", {"start": v(-302.4, 96.1) * mm, "end": v(-235.21, 96.1) * mm});
            skLineSegment(sketch, "E648", {"start": v(-168.02, 96.1) * mm, "end": v(-101.6, 96.1) * mm});
            skLineSegment(sketch, "E649", {"start": v(101.6, 96.1) * mm, "end": v(167.93, 96.1) * mm});
            skLineSegment(sketch, "E650", {"start": v(235.12, 96.1) * mm, "end": v(302.31, 96.1) * mm});
            skLineSegment(sketch, "E651", {"start": v(369.5, 96.1) * mm, "end": v(436.7, 96.1) * mm});
            skLineSegment(sketch, "E652", {"start": v(-436.79, 58) * mm, "end": v(-436.79, 96.1) * mm});
            skLineSegment(sketch, "E653", {"start": v(-369.6, 58) * mm, "end": v(-369.6, 96.1) * mm});
            skLineSegment(sketch, "E654", {"start": v(-302.4, 58) * mm, "end": v(-302.4, 96.1) * mm});
            skLineSegment(sketch, "E655", {"start": v(-235.21, 58) * mm, "end": v(-235.21, 96.1) * mm});
            skLineSegment(sketch, "E656", {"start": v(-168.02, 58) * mm, "end": v(-168.02, 96.1) * mm});
            skLineSegment(sketch, "E657", {"start": v(167.93, 58) * mm, "end": v(167.93, 96.1) * mm});
            skLineSegment(sketch, "E658", {"start": v(235.12, 58) * mm, "end": v(235.12, 96.1) * mm});
            skLineSegment(sketch, "E659", {"start": v(302.31, 58) * mm, "end": v(302.31, 96.1) * mm});
            skLineSegment(sketch, "E660", {"start": v(369.5, 58) * mm, "end": v(369.5, 96.1) * mm});
            skLineSegment(sketch, "E661", {"start": v(-496.62, 58) * mm, "end": v(-436.79, 58) * mm});
            skLineSegment(sketch, "E662", {"start": v(-369.6, 58) * mm, "end": v(-302.4, 58) * mm});
            skLineSegment(sketch, "E663", {"start": v(-235.21, 58) * mm, "end": v(-168.02, 58) * mm});
            skLineSegment(sketch, "E664", {"start": v(302.31, 58) * mm, "end": v(369.5, 58) * mm});
            skLineSegment(sketch, "E665", {"start": v(436.7, 58) * mm, "end": v(496.52, 58) * mm});
            skLineSegment(sketch, "E666", {"start": v(167.93, 58) * mm, "end": v(235.12, 58) * mm});
            skLineSegment(sketch, "E667", {"start": v(436.7, 96.1) * mm, "end": v(436.7, 58) * mm});
            skLineSegment(sketch, "E668", {"start": v(-508.99, 19.9) * mm, "end": v(-430.69, 19.9) * mm});
            skLineSegment(sketch, "E669", {"start": v(-352.39, 19.9) * mm, "end": v(-274.09, 19.9) * mm});
            skLineSegment(sketch, "E670", {"start": v(-195.79, 19.9) * mm, "end": v(-117.49, 19.9) * mm});
            skLineSegment(sketch, "E671", {"start": v(117.41, 19.9) * mm, "end": v(195.71, 19.9) * mm});
            skLineSegment(sketch, "E672", {"start": v(274.01, 19.9) * mm, "end": v(352.31, 19.9) * mm});
            skLineSegment(sketch, "E673", {"start": v(430.61, 19.9) * mm, "end": v(508.91, 19.9) * mm});
            skLineSegment(sketch, "E674", {"start": v(-508.99, -18.2) * mm, "end": v(-508.99, 19.9) * mm});
            skLineSegment(sketch, "E675", {"start": v(-430.69, -18.2) * mm, "end": v(-430.69, 19.9) * mm});
            skLineSegment(sketch, "E676", {"start": v(-352.39, -18.2) * mm, "end": v(-352.39, 19.9) * mm});
            skLineSegment(sketch, "E677", {"start": v(-274.09, -18.2) * mm, "end": v(-274.09, 19.9) * mm});
            skLineSegment(sketch, "E678", {"start": v(-195.79, -18.2) * mm, "end": v(-195.79, 19.9) * mm});
            skLineSegment(sketch, "E679", {"start": v(-117.49, -18.2) * mm, "end": v(-117.49, 19.9) * mm});
            skLineSegment(sketch, "E680", {"start": v(117.41, -18.2) * mm, "end": v(117.41, 19.9) * mm});
            skLineSegment(sketch, "E681", {"start": v(195.71, -18.2) * mm, "end": v(195.71, 19.9) * mm});
            skLineSegment(sketch, "E682", {"start": v(274.01, -18.2) * mm, "end": v(274.01, 19.9) * mm});
            skLineSegment(sketch, "E683", {"start": v(352.31, -18.2) * mm, "end": v(352.31, 19.9) * mm});
            skLineSegment(sketch, "E684", {"start": v(430.61, -18.2) * mm, "end": v(430.61, 19.9) * mm});
            skLineSegment(sketch, "E685", {"start": v(-578.71, -18.2) * mm, "end": v(-508.99, -18.2) * mm});
            skLineSegment(sketch, "E686", {"start": v(-430.69, -18.2) * mm, "end": v(-352.39, -18.2) * mm});
            skLineSegment(sketch, "E687", {"start": v(-274.09, -18.2) * mm, "end": v(-195.79, -18.2) * mm});
            skLineSegment(sketch, "E688", {"start": v(-117.49, -18.2) * mm, "end": v(-101.6, -18.2) * mm});
            skLineSegment(sketch, "E689", {"start": v(101.6, -18.2) * mm, "end": v(117.41, -18.2) * mm});
            skLineSegment(sketch, "E690", {"start": v(352.31, -18.2) * mm, "end": v(430.61, -18.2) * mm});
            skLineSegment(sketch, "E691", {"start": v(508.91, -18.2) * mm, "end": v(578.63, -18.2) * mm});
            skLineSegment(sketch, "E692", {"start": v(195.71, -18.2) * mm, "end": v(274.01, -18.2) * mm});
            skLineSegment(sketch, "E693", {"start": v(508.91, 19.9) * mm, "end": v(508.91, -18.2) * mm});
            skLineSegment(sketch, "E694", {"start": v(-581.2, -56.3) * mm, "end": v(-491.78, -56.3) * mm});
            skLineSegment(sketch, "E695", {"start": v(-402.37, -56.3) * mm, "end": v(-312.96, -56.3) * mm});
            skLineSegment(sketch, "E696", {"start": v(-223.55, -56.3) * mm, "end": v(-134.15, -56.3) * mm});
            skLineSegment(sketch, "E697", {"start": v(134.08, -56.3) * mm, "end": v(223.5, -56.3) * mm});
            skLineSegment(sketch, "E698", {"start": v(312.9, -56.3) * mm, "end": v(402.3, -56.3) * mm});
            skLineSegment(sketch, "E699", {"start": v(491.72, -56.3) * mm, "end": v(581.13, -56.3) * mm});
            skLineSegment(sketch, "E700", {"start": v(-581.2, -94.4) * mm, "end": v(-581.2, -56.3) * mm});
            skLineSegment(sketch, "E701", {"start": v(-491.78, -94.4) * mm, "end": v(-491.78, -56.3) * mm});
            skLineSegment(sketch, "E702", {"start": v(-402.37, -94.4) * mm, "end": v(-402.37, -56.3) * mm});
            skLineSegment(sketch, "E703", {"start": v(-312.96, -94.4) * mm, "end": v(-312.96, -56.3) * mm});
            skLineSegment(sketch, "E704", {"start": v(-223.55, -94.4) * mm, "end": v(-223.55, -56.3) * mm});
            skLineSegment(sketch, "E705", {"start": v(-134.15, -94.4) * mm, "end": v(-134.15, -56.3) * mm});
            skLineSegment(sketch, "E706", {"start": v(134.08, -94.4) * mm, "end": v(134.08, -56.3) * mm});
            skLineSegment(sketch, "E707", {"start": v(223.5, -94.4) * mm, "end": v(223.5, -56.3) * mm});
            skLineSegment(sketch, "E708", {"start": v(312.9, -94.4) * mm, "end": v(312.9, -56.3) * mm});
            skLineSegment(sketch, "E709", {"start": v(402.3, -94.4) * mm, "end": v(402.3, -56.3) * mm});
            skLineSegment(sketch, "E710", {"start": v(491.72, -94.4) * mm, "end": v(491.72, -56.3) * mm});
            skLineSegment(sketch, "E711", {"start": v(-660.8, -94.4) * mm, "end": v(-581.2, -94.4) * mm});
            skLineSegment(sketch, "E712", {"start": v(-491.78, -94.4) * mm, "end": v(-402.37, -94.4) * mm});
            skLineSegment(sketch, "E713", {"start": v(-312.96, -94.4) * mm, "end": v(-223.55, -94.4) * mm});
            skLineSegment(sketch, "E714", {"start": v(-134.15, -94.4) * mm, "end": v(-101.6, -94.4) * mm});
            skLineSegment(sketch, "E715", {"start": v(101.6, -94.4) * mm, "end": v(134.08, -94.4) * mm});
            skLineSegment(sketch, "E716", {"start": v(402.3, -94.4) * mm, "end": v(491.72, -94.4) * mm});
            skLineSegment(sketch, "E717", {"start": v(581.13, -94.4) * mm, "end": v(660.74, -94.4) * mm});
            skLineSegment(sketch, "E718", {"start": v(223.5, -94.4) * mm, "end": v(312.9, -94.4) * mm});
            skLineSegment(sketch, "E719", {"start": v(581.13, -56.3) * mm, "end": v(581.13, -94.4) * mm});
            skLineSegment(sketch, "E720", {"start": v(-653.4, -132.5) * mm, "end": v(-552.87, -132.5) * mm});
            skLineSegment(sketch, "E721", {"start": v(-452.36, -132.5) * mm, "end": v(-351.84, -132.5) * mm});
            skLineSegment(sketch, "E722", {"start": v(-251.32, -132.5) * mm, "end": v(-150.8, -132.5) * mm});
            skLineSegment(sketch, "E723", {"start": v(150.75, -132.5) * mm, "end": v(251.27, -132.5) * mm});
            skLineSegment(sketch, "E724", {"start": v(351.8, -132.5) * mm, "end": v(452.3, -132.5) * mm});
            skLineSegment(sketch, "E725", {"start": v(552.83, -132.5) * mm, "end": v(653.35, -132.5) * mm});
            skLineSegment(sketch, "E726", {"start": v(-653.4, -170.6) * mm, "end": v(-653.4, -132.5) * mm});
            skLineSegment(sketch, "E727", {"start": v(-552.87, -170.6) * mm, "end": v(-552.87, -132.5) * mm});
            skLineSegment(sketch, "E728", {"start": v(-452.36, -170.6) * mm, "end": v(-452.36, -132.5) * mm});
            skLineSegment(sketch, "E729", {"start": v(-351.84, -170.6) * mm, "end": v(-351.84, -132.5) * mm});
            skLineSegment(sketch, "E730", {"start": v(-251.32, -170.6) * mm, "end": v(-251.32, -132.5) * mm});
            skLineSegment(sketch, "E731", {"start": v(-150.8, -170.6) * mm, "end": v(-150.8, -132.5) * mm});
            skLineSegment(sketch, "E732", {"start": v(150.75, -170.6) * mm, "end": v(150.75, -132.5) * mm});
            skLineSegment(sketch, "E733", {"start": v(251.27, -170.6) * mm, "end": v(251.27, -132.5) * mm});
            skLineSegment(sketch, "E734", {"start": v(351.8, -170.6) * mm, "end": v(351.8, -132.5) * mm});
            skLineSegment(sketch, "E735", {"start": v(452.3, -170.6) * mm, "end": v(452.3, -132.5) * mm});
            skLineSegment(sketch, "E736", {"start": v(552.83, -170.6) * mm, "end": v(552.83, -132.5) * mm});
            skLineSegment(sketch, "E737", {"start": v(-742.9, -170.6) * mm, "end": v(-653.4, -170.6) * mm});
            skLineSegment(sketch, "E738", {"start": v(-552.87, -170.6) * mm, "end": v(-452.36, -170.6) * mm});
            skLineSegment(sketch, "E739", {"start": v(-351.84, -170.6) * mm, "end": v(-251.32, -170.6) * mm});
            skLineSegment(sketch, "E740", {"start": v(-150.8, -170.6) * mm, "end": v(-101.6, -170.6) * mm});
            skLineSegment(sketch, "E741", {"start": v(101.6, -170.6) * mm, "end": v(150.75, -170.6) * mm});
            skLineSegment(sketch, "E742", {"start": v(452.3, -170.6) * mm, "end": v(552.83, -170.6) * mm});
            skLineSegment(sketch, "E743", {"start": v(653.35, -170.6) * mm, "end": v(742.85, -170.6) * mm});
            skLineSegment(sketch, "E744", {"start": v(251.27, -170.6) * mm, "end": v(351.8, -170.6) * mm});
            skLineSegment(sketch, "E745", {"start": v(653.35, -132.5) * mm, "end": v(653.35, -170.6) * mm});
            skLineSegment(sketch, "E746", {"start": v(-725.6, -208.7) * mm, "end": v(-613.97, -208.7) * mm});
            skLineSegment(sketch, "E747", {"start": v(-502.34, -208.7) * mm, "end": v(-390.71, -208.7) * mm});
            skLineSegment(sketch, "E748", {"start": v(-279.08, -208.7) * mm, "end": v(-167.46, -208.7) * mm});
            skLineSegment(sketch, "E749", {"start": v(167.43, -208.7) * mm, "end": v(279.05, -208.7) * mm});
            skLineSegment(sketch, "E750", {"start": v(390.68, -208.7) * mm, "end": v(502.3, -208.7) * mm});
            skLineSegment(sketch, "E751", {"start": v(613.94, -208.7) * mm, "end": v(725.56, -208.7) * mm});
            skLineSegment(sketch, "E752", {"start": v(-725.6, -246.8) * mm, "end": v(-725.6, -208.7) * mm});
            skLineSegment(sketch, "E753", {"start": v(-613.97, -246.8) * mm, "end": v(-613.97, -208.7) * mm});
            skLineSegment(sketch, "E754", {"start": v(-502.34, -246.8) * mm, "end": v(-502.34, -208.7) * mm});
            skLineSegment(sketch, "E755", {"start": v(-390.71, -246.8) * mm, "end": v(-390.71, -208.7) * mm});
            skLineSegment(sketch, "E756", {"start": v(-279.08, -246.8) * mm, "end": v(-279.08, -208.7) * mm});
            skLineSegment(sketch, "E757", {"start": v(-167.46, -246.8) * mm, "end": v(-167.46, -208.7) * mm});
            skLineSegment(sketch, "E758", {"start": v(167.43, -246.8) * mm, "end": v(167.43, -208.7) * mm});
            skLineSegment(sketch, "E759", {"start": v(279.05, -246.8) * mm, "end": v(279.05, -208.7) * mm});
            skLineSegment(sketch, "E760", {"start": v(390.68, -246.8) * mm, "end": v(390.68, -208.7) * mm});
            skLineSegment(sketch, "E761", {"start": v(502.3, -246.8) * mm, "end": v(502.3, -208.7) * mm});
            skLineSegment(sketch, "E762", {"start": v(613.94, -246.8) * mm, "end": v(613.94, -208.7) * mm});
            skLineSegment(sketch, "E763", {"start": v(-825, -246.8) * mm, "end": v(-725.6, -246.8) * mm});
            skLineSegment(sketch, "E764", {"start": v(-613.97, -246.8) * mm, "end": v(-502.34, -246.8) * mm});
            skLineSegment(sketch, "E765", {"start": v(-390.71, -246.8) * mm, "end": v(-279.08, -246.8) * mm});
            skLineSegment(sketch, "E766", {"start": v(-167.46, -246.8) * mm, "end": v(-101.6, -246.8) * mm});
            skLineSegment(sketch, "E767", {"start": v(101.6, -246.8) * mm, "end": v(167.43, -246.8) * mm});
            skLineSegment(sketch, "E768", {"start": v(502.3, -246.8) * mm, "end": v(613.94, -246.8) * mm});
            skLineSegment(sketch, "E769", {"start": v(725.56, -246.8) * mm, "end": v(824.96, -246.8) * mm});
            skLineSegment(sketch, "E770", {"start": v(279.05, -246.8) * mm, "end": v(390.68, -246.8) * mm});
            skLineSegment(sketch, "E771", {"start": v(725.56, -208.7) * mm, "end": v(725.56, -246.8) * mm});
            skLineSegment(sketch, "E772", {"start": v(-797.8, -284.9) * mm, "end": v(-675.06, -284.9) * mm});
            skLineSegment(sketch, "E773", {"start": v(-552.32, -284.9) * mm, "end": v(-429.59, -284.9) * mm});
            skLineSegment(sketch, "E774", {"start": v(-306.85, -284.9) * mm, "end": v(-184.11, -284.9) * mm});
            skLineSegment(sketch, "E775", {"start": v(184.1, -284.9) * mm, "end": v(306.83, -284.9) * mm});
            skLineSegment(sketch, "E776", {"start": v(429.57, -284.9) * mm, "end": v(552.3, -284.9) * mm});
            skLineSegment(sketch, "E777", {"start": v(675.04, -284.9) * mm, "end": v(797.78, -284.9) * mm});
            skLineSegment(sketch, "E778", {"start": v(-797.8, -323) * mm, "end": v(-797.8, -284.9) * mm});
            skLineSegment(sketch, "E779", {"start": v(-675.06, -323) * mm, "end": v(-675.06, -284.9) * mm});
            skLineSegment(sketch, "E780", {"start": v(-552.32, -323) * mm, "end": v(-552.32, -284.9) * mm});
            skLineSegment(sketch, "E781", {"start": v(-429.59, -323) * mm, "end": v(-429.59, -284.9) * mm});
            skLineSegment(sketch, "E782", {"start": v(-306.85, -323) * mm, "end": v(-306.85, -284.9) * mm});
            skLineSegment(sketch, "E783", {"start": v(-184.11, -323) * mm, "end": v(-184.11, -284.9) * mm});
            skLineSegment(sketch, "E784", {"start": v(184.1, -323) * mm, "end": v(184.1, -284.9) * mm});
            skLineSegment(sketch, "E785", {"start": v(306.83, -323) * mm, "end": v(306.83, -284.9) * mm});
            skLineSegment(sketch, "E786", {"start": v(429.57, -323) * mm, "end": v(429.57, -284.9) * mm});
            skLineSegment(sketch, "E787", {"start": v(552.3, -323) * mm, "end": v(552.3, -284.9) * mm});
            skLineSegment(sketch, "E788", {"start": v(675.04, -323) * mm, "end": v(675.04, -284.9) * mm});
            skLineSegment(sketch, "E789", {"start": v(-907.09, -323) * mm, "end": v(-797.8, -323) * mm});
            skLineSegment(sketch, "E790", {"start": v(-675.06, -323) * mm, "end": v(-552.32, -323) * mm});
            skLineSegment(sketch, "E791", {"start": v(-429.59, -323) * mm, "end": v(-306.85, -323) * mm});
            skLineSegment(sketch, "E792", {"start": v(-184.11, -323) * mm, "end": v(-101.6, -323) * mm});
            skLineSegment(sketch, "E793", {"start": v(101.6, -323) * mm, "end": v(184.1, -323) * mm});
            skLineSegment(sketch, "E794", {"start": v(552.3, -323) * mm, "end": v(675.04, -323) * mm});
            skLineSegment(sketch, "E795", {"start": v(797.78, -323) * mm, "end": v(907.07, -323) * mm});
            skLineSegment(sketch, "E796", {"start": v(306.83, -323) * mm, "end": v(429.57, -323) * mm});
            skLineSegment(sketch, "E797", {"start": v(797.78, -284.9) * mm, "end": v(797.78, -323) * mm});
            skLineSegment(sketch, "E798", {"start": v(-57.15, 312) * mm, "end": v(-57.15, 305.65) * mm});
            skLineSegment(sketch, "E799", {"start": v(-31.75, 312) * mm, "end": v(-31.75, 305.65) * mm});
            skLineSegment(sketch, "E800", {"start": v(31.75, 312) * mm, "end": v(31.75, 305.65) * mm});
            skLineSegment(sketch, "E801", {"start": v(57.15, 312) * mm, "end": v(57.15, 305.65) * mm});
            skLineSegment(sketch, "E802", {"start": v(38.1, 305.65) * mm, "end": v(31.75, 305.65) * mm});
            skLineSegment(sketch, "E803", {"start": v(-50.8, 305.65) * mm, "end": v(-57.15, 305.65) * mm});
            skLineSegment(sketch, "E804", {"start": v(57.15, 305.65) * mm, "end": v(50.8, 305.65) * mm});
            skLineSegment(sketch, "E805", {"start": v(-31.75, 305.65) * mm, "end": v(-38.1, 305.65) * mm});
            skLineSegment(sketch, "E806", {"start": v(-267.55, 415.07) * mm, "end": v(-273.05, 424.6) * mm});
            skLineSegment(sketch, "E807", {"start": v(267.55, 415.07) * mm, "end": v(273.05, 424.6) * mm});
            skLineSegment(sketch, "E808", {"start": v(273.05, 424.6) * mm, "end": v(-273.05, 424.6) * mm});
            skLineSegment(sketch, "E809", {"start": v(-266.7, 324.48) * mm, "end": v(266.7, 324.48) * mm});
            skLineSegment(sketch, "E810", {"start": v(-266.7, 354.13) * mm, "end": v(-266.7, 324.48) * mm});
            skLineSegment(sketch, "E811", {"start": v(-23.24, 381.85) * mm, "end": v(23.24, 381.85) * mm});
            skLineSegment(sketch, "E812", {"start": v(23.24, 381.85) * mm, "end": v(23.24, 369.15) * mm});
            skLineSegment(sketch, "E813", {"start": v(23.24, 369.15) * mm, "end": v(-23.24, 369.15) * mm});
            skLineSegment(sketch, "E814", {"start": v(-23.24, 381.85) * mm, "end": v(-23.24, 369.15) * mm});
            skLineSegment(sketch, "E815", {"start": v(180.6, 369.15) * mm, "end": v(180.6, 381.85) * mm});
            skLineSegment(sketch, "E816", {"start": v(-180.6, 381.85) * mm, "end": v(-180.6, 369.15) * mm});
            skLineSegment(sketch, "E817", {"start": v(-127.25, 381.85) * mm, "end": v(-127.25, 369.15) * mm});
            skLineSegment(sketch, "E818", {"start": v(127.25, 369.15) * mm, "end": v(127.25, 381.85) * mm});
            skLineSegment(sketch, "E819", {"start": v(-127.25, 381.85) * mm, "end": v(-180.6, 381.85) * mm});
            skLineSegment(sketch, "E820", {"start": v(-127.25, 369.15) * mm, "end": v(-180.6, 369.15) * mm});
            skLineSegment(sketch, "E821", {"start": v(127.25, 381.85) * mm, "end": v(180.6, 381.85) * mm});
            skLineSegment(sketch, "E822", {"start": v(127.25, 369.15) * mm, "end": v(180.6, 369.15) * mm});
            skLineSegment(sketch, "E823", {"start": v(-254, 283.65) * mm, "end": v(-76.2, 283.65) * mm});
            skLineSegment(sketch, "E824", {"start": v(-255.7, 277.3) * mm, "end": v(-76.2, 277.3) * mm});
            skLineSegment(sketch, "E825", {"start": v(254, 283.65) * mm, "end": v(76.2, 283.65) * mm});
            skLineSegment(sketch, "E826", {"start": v(255.7, 277.3) * mm, "end": v(76.2, 277.3) * mm});
            skLineSegment(sketch, "E827", {"start": v(266.7, 354.13) * mm, "end": v(266.7, 324.48) * mm});
            skArc(sketch, "E828", {"start": v(267.55, 415.07) * mm, "mid": v(266.92, 413.54) * mm, "end": v(266.7, 411.9) * mm});
            skArc(sketch, "E829", {"start": v(-266.7, 411.9) * mm, "mid": v(-266.92, 413.54) * mm, "end": v(-267.55, 415.07) * mm});
            skLineSegment(sketch, "E830", {"start": v(-266.7, 411.9) * mm, "end": v(266.7, 411.9) * mm});
            skLineSegment(sketch, "E831", {"start": v(267.55, 415.07) * mm, "end": v(-267.55, 415.07) * mm});
            skLineSegment(sketch, "E832", {"start": v(101.6, -424.6) * mm, "end": v(101.6, 261.2) * mm});
            skLineSegment(sketch, "E833", {"start": v(-101.6, -424.6) * mm, "end": v(-101.6, 261.2) * mm});
            skLineSegment(sketch, "E834", {"start": v(-76.2, -424.6) * mm, "end": v(-76.2, 261.2) * mm});
            skLineSegment(sketch, "E835", {"start": v(76.2, -424.6) * mm, "end": v(76.2, 261.2) * mm});
            skLineSegment(sketch, "E836", {"start": v(-76.2, 261.2) * mm, "end": v(50.8, 261.2) * mm});
            skLineSegment(sketch, "E837", {"start": v(50.8, 253.66) * mm, "end": v(76.2, 253.66) * mm});
            skLineSegment(sketch, "E838", {"start": v(-76.2, 253.66) * mm, "end": v(50.8, 253.66) * mm});
            skLineSegment(sketch, "E839", {"start": v(50.8, 246.11) * mm, "end": v(76.2, 246.11) * mm});
            skLineSegment(sketch, "E840", {"start": v(-76.2, 246.11) * mm, "end": v(50.8, 246.11) * mm});
            skLineSegment(sketch, "E841", {"start": v(50.8, 238.57) * mm, "end": v(76.2, 238.57) * mm});
            skLineSegment(sketch, "E842", {"start": v(-76.2, 238.57) * mm, "end": v(50.8, 238.57) * mm});
            skLineSegment(sketch, "E843", {"start": v(50.8, 231.03) * mm, "end": v(76.2, 231.03) * mm});
            skLineSegment(sketch, "E844", {"start": v(-76.2, 231.03) * mm, "end": v(50.8, 231.03) * mm});
            skLineSegment(sketch, "E845", {"start": v(50.8, 223.48) * mm, "end": v(76.2, 223.48) * mm});
            skLineSegment(sketch, "E846", {"start": v(-76.2, 223.48) * mm, "end": v(50.8, 223.48) * mm});
            skLineSegment(sketch, "E847", {"start": v(50.8, 215.94) * mm, "end": v(76.2, 215.94) * mm});
            skLineSegment(sketch, "E848", {"start": v(-76.2, 215.94) * mm, "end": v(50.8, 215.94) * mm});
            skLineSegment(sketch, "E849", {"start": v(50.8, 208.4) * mm, "end": v(76.2, 208.4) * mm});
            skLineSegment(sketch, "E850", {"start": v(-76.2, 208.4) * mm, "end": v(50.8, 208.4) * mm});
            skLineSegment(sketch, "E851", {"start": v(50.8, 200.85) * mm, "end": v(76.2, 200.85) * mm});
            skLineSegment(sketch, "E852", {"start": v(-76.2, 200.85) * mm, "end": v(50.8, 200.85) * mm});
            skLineSegment(sketch, "E853", {"start": v(50.8, 193.3) * mm, "end": v(76.2, 193.3) * mm});
            skLineSegment(sketch, "E854", {"start": v(-76.2, 193.3) * mm, "end": v(50.8, 193.3) * mm});
            skLineSegment(sketch, "E855", {"start": v(50.8, 185.76) * mm, "end": v(76.2, 185.76) * mm});
            skLineSegment(sketch, "E856", {"start": v(-76.2, 185.76) * mm, "end": v(50.8, 185.76) * mm});
            skLineSegment(sketch, "E857", {"start": v(50.8, 178.22) * mm, "end": v(76.2, 178.22) * mm});
            skLineSegment(sketch, "E858", {"start": v(-76.2, 178.22) * mm, "end": v(50.8, 178.22) * mm});
            skLineSegment(sketch, "E859", {"start": v(50.8, 170.68) * mm, "end": v(76.2, 170.68) * mm});
            skLineSegment(sketch, "E860", {"start": v(-76.2, 170.68) * mm, "end": v(50.8, 170.68) * mm});
            skLineSegment(sketch, "E861", {"start": v(50.8, 163.13) * mm, "end": v(76.2, 163.13) * mm});
            skLineSegment(sketch, "E862", {"start": v(-76.2, 163.13) * mm, "end": v(50.8, 163.13) * mm});
            skLineSegment(sketch, "E863", {"start": v(50.8, 155.59) * mm, "end": v(76.2, 155.59) * mm});
            skLineSegment(sketch, "E864", {"start": v(-76.2, 155.59) * mm, "end": v(50.8, 155.59) * mm});
            skLineSegment(sketch, "E865", {"start": v(50.8, 148.04) * mm, "end": v(76.2, 148.04) * mm});
            skLineSegment(sketch, "E866", {"start": v(-76.2, 148.04) * mm, "end": v(50.8, 148.04) * mm});
            skLineSegment(sketch, "E867", {"start": v(50.8, 140.5) * mm, "end": v(76.2, 140.5) * mm});
            skLineSegment(sketch, "E868", {"start": v(-76.2, 140.5) * mm, "end": v(50.8, 140.5) * mm});
            skLineSegment(sketch, "E869", {"start": v(50.8, 132.96) * mm, "end": v(76.2, 132.96) * mm});
            skLineSegment(sketch, "E870", {"start": v(-76.2, 132.96) * mm, "end": v(50.8, 132.96) * mm});
            skLineSegment(sketch, "E871", {"start": v(50.8, 125.41) * mm, "end": v(76.2, 125.41) * mm});
            skLineSegment(sketch, "E872", {"start": v(-76.2, 125.41) * mm, "end": v(50.8, 125.41) * mm});
            skLineSegment(sketch, "E873", {"start": v(50.8, 117.87) * mm, "end": v(76.2, 117.87) * mm});
            skLineSegment(sketch, "E874", {"start": v(-76.2, 117.87) * mm, "end": v(50.8, 117.87) * mm});
            skLineSegment(sketch, "E875", {"start": v(50.8, 110.32) * mm, "end": v(76.2, 110.32) * mm});
            skLineSegment(sketch, "E876", {"start": v(-76.2, 110.32) * mm, "end": v(50.8, 110.32) * mm});
            skLineSegment(sketch, "E877", {"start": v(50.8, 102.78) * mm, "end": v(76.2, 102.78) * mm});
            skLineSegment(sketch, "E878", {"start": v(-76.2, 102.78) * mm, "end": v(50.8, 102.78) * mm});
            skLineSegment(sketch, "E879", {"start": v(50.8, 95.24) * mm, "end": v(76.2, 95.24) * mm});
            skLineSegment(sketch, "E880", {"start": v(-76.2, 95.24) * mm, "end": v(50.8, 95.24) * mm});
            skLineSegment(sketch, "E881", {"start": v(50.8, 87.7) * mm, "end": v(76.2, 87.7) * mm});
            skLineSegment(sketch, "E882", {"start": v(-76.2, 87.7) * mm, "end": v(50.8, 87.7) * mm});
            skLineSegment(sketch, "E883", {"start": v(50.8, 80.15) * mm, "end": v(76.2, 80.15) * mm});
            skLineSegment(sketch, "E884", {"start": v(-76.2, 80.15) * mm, "end": v(50.8, 80.15) * mm});
            skLineSegment(sketch, "E885", {"start": v(50.8, 72.6) * mm, "end": v(76.2, 72.6) * mm});
            skLineSegment(sketch, "E886", {"start": v(-76.2, 72.6) * mm, "end": v(50.8, 72.6) * mm});
            skLineSegment(sketch, "E887", {"start": v(50.8, 65.06) * mm, "end": v(76.2, 65.06) * mm});
            skLineSegment(sketch, "E888", {"start": v(-76.2, 65.06) * mm, "end": v(50.8, 65.06) * mm});
            skLineSegment(sketch, "E889", {"start": v(50.8, 57.52) * mm, "end": v(76.2, 57.52) * mm});
            skLineSegment(sketch, "E890", {"start": v(-76.2, 57.52) * mm, "end": v(50.8, 57.52) * mm});
            skLineSegment(sketch, "E891", {"start": v(50.8, 49.97) * mm, "end": v(76.2, 49.97) * mm});
            skLineSegment(sketch, "E892", {"start": v(-76.2, 49.97) * mm, "end": v(50.8, 49.97) * mm});
            skLineSegment(sketch, "E893", {"start": v(50.8, 42.43) * mm, "end": v(76.2, 42.43) * mm});
            skLineSegment(sketch, "E894", {"start": v(-76.2, 42.43) * mm, "end": v(50.8, 42.43) * mm});
            skLineSegment(sketch, "E895", {"start": v(50.8, 34.89) * mm, "end": v(76.2, 34.89) * mm});
            skLineSegment(sketch, "E896", {"start": v(-76.2, 34.89) * mm, "end": v(50.8, 34.89) * mm});
            skLineSegment(sketch, "E897", {"start": v(50.8, 27.34) * mm, "end": v(76.2, 27.34) * mm});
            skLineSegment(sketch, "E898", {"start": v(-76.2, 27.34) * mm, "end": v(50.8, 27.34) * mm});
            skLineSegment(sketch, "E899", {"start": v(50.8, 19.8) * mm, "end": v(76.2, 19.8) * mm});
            skLineSegment(sketch, "E900", {"start": v(-76.2, 19.8) * mm, "end": v(50.8, 19.8) * mm});
            skLineSegment(sketch, "E901", {"start": v(50.8, 12.26) * mm, "end": v(76.2, 12.26) * mm});
            skLineSegment(sketch, "E902", {"start": v(-76.2, 12.26) * mm, "end": v(50.8, 12.26) * mm});
            skLineSegment(sketch, "E903", {"start": v(50.8, 4.71) * mm, "end": v(76.2, 4.71) * mm});
            skLineSegment(sketch, "E904", {"start": v(-76.2, 4.71) * mm, "end": v(50.8, 4.71) * mm});
            skLineSegment(sketch, "E905", {"start": v(50.8, -2.83) * mm, "end": v(76.2, -2.83) * mm});
            skLineSegment(sketch, "E906", {"start": v(-76.2, -2.83) * mm, "end": v(50.8, -2.83) * mm});
            skLineSegment(sketch, "E907", {"start": v(50.8, -10.38) * mm, "end": v(76.2, -10.38) * mm});
            skLineSegment(sketch, "E908", {"start": v(-76.2, -10.38) * mm, "end": v(50.8, -10.38) * mm});
            skLineSegment(sketch, "E909", {"start": v(50.8, -17.92) * mm, "end": v(76.2, -17.92) * mm});
            skLineSegment(sketch, "E910", {"start": v(-76.2, -17.92) * mm, "end": v(50.8, -17.92) * mm});
            skLineSegment(sketch, "E911", {"start": v(50.8, -25.46) * mm, "end": v(76.2, -25.46) * mm});
            skLineSegment(sketch, "E912", {"start": v(-76.2, -25.46) * mm, "end": v(50.8, -25.46) * mm});
            skLineSegment(sketch, "E913", {"start": v(50.8, -33) * mm, "end": v(76.2, -33) * mm});
            skLineSegment(sketch, "E914", {"start": v(-76.2, -33) * mm, "end": v(50.8, -33) * mm});
            skLineSegment(sketch, "E915", {"start": v(50.8, -40.55) * mm, "end": v(76.2, -40.55) * mm});
            skLineSegment(sketch, "E916", {"start": v(-76.2, -40.55) * mm, "end": v(50.8, -40.55) * mm});
            skLineSegment(sketch, "E917", {"start": v(50.8, -48.1) * mm, "end": v(76.2, -48.1) * mm});
            skLineSegment(sketch, "E918", {"start": v(-76.2, -48.1) * mm, "end": v(50.8, -48.1) * mm});
            skLineSegment(sketch, "E919", {"start": v(50.8, -55.64) * mm, "end": v(76.2, -55.64) * mm});
            skLineSegment(sketch, "E920", {"start": v(-76.2, -55.64) * mm, "end": v(50.8, -55.64) * mm});
            skLineSegment(sketch, "E921", {"start": v(50.8, -63.18) * mm, "end": v(76.2, -63.18) * mm});
            skLineSegment(sketch, "E922", {"start": v(-76.2, -63.18) * mm, "end": v(50.8, -63.18) * mm});
            skLineSegment(sketch, "E923", {"start": v(50.8, -70.73) * mm, "end": v(76.2, -70.73) * mm});
            skLineSegment(sketch, "E924", {"start": v(-76.2, -70.73) * mm, "end": v(50.8, -70.73) * mm});
            skLineSegment(sketch, "E925", {"start": v(50.8, -78.27) * mm, "end": v(76.2, -78.27) * mm});
            skLineSegment(sketch, "E926", {"start": v(-76.2, -78.27) * mm, "end": v(50.8, -78.27) * mm});
            skLineSegment(sketch, "E927", {"start": v(50.8, -85.81) * mm, "end": v(76.2, -85.81) * mm});
            skLineSegment(sketch, "E928", {"start": v(-76.2, -85.81) * mm, "end": v(50.8, -85.81) * mm});
            skLineSegment(sketch, "E929", {"start": v(50.8, -93.36) * mm, "end": v(76.2, -93.36) * mm});
            skLineSegment(sketch, "E930", {"start": v(-76.2, -93.36) * mm, "end": v(50.8, -93.36) * mm});
            skLineSegment(sketch, "E931", {"start": v(50.8, -100.9) * mm, "end": v(76.2, -100.9) * mm});
            skLineSegment(sketch, "E932", {"start": v(-76.2, -100.9) * mm, "end": v(50.8, -100.9) * mm});
            skLineSegment(sketch, "E933", {"start": v(50.8, -108.45) * mm, "end": v(76.2, -108.45) * mm});
            skLineSegment(sketch, "E934", {"start": v(-76.2, -108.45) * mm, "end": v(50.8, -108.45) * mm});
            skLineSegment(sketch, "E935", {"start": v(50.8, -115.99) * mm, "end": v(76.2, -115.99) * mm});
            skLineSegment(sketch, "E936", {"start": v(-76.2, -115.99) * mm, "end": v(50.8, -115.99) * mm});
            skLineSegment(sketch, "E937", {"start": v(50.8, -123.53) * mm, "end": v(76.2, -123.53) * mm});
            skLineSegment(sketch, "E938", {"start": v(-76.2, -123.53) * mm, "end": v(50.8, -123.53) * mm});
            skLineSegment(sketch, "E939", {"start": v(50.8, -131.08) * mm, "end": v(76.2, -131.08) * mm});
            skLineSegment(sketch, "E940", {"start": v(-76.2, -131.08) * mm, "end": v(50.8, -131.08) * mm});
            skLineSegment(sketch, "E941", {"start": v(50.8, -138.62) * mm, "end": v(76.2, -138.62) * mm});
            skLineSegment(sketch, "E942", {"start": v(-76.2, -138.62) * mm, "end": v(50.8, -138.62) * mm});
            skLineSegment(sketch, "E943", {"start": v(50.8, -146.16) * mm, "end": v(76.2, -146.16) * mm});
            skLineSegment(sketch, "E944", {"start": v(-76.2, -146.16) * mm, "end": v(50.8, -146.16) * mm});
            skLineSegment(sketch, "E945", {"start": v(50.8, -153.7) * mm, "end": v(76.2, -153.7) * mm});
            skLineSegment(sketch, "E946", {"start": v(-76.2, -153.7) * mm, "end": v(50.8, -153.7) * mm});
            skLineSegment(sketch, "E947", {"start": v(50.8, -161.25) * mm, "end": v(76.2, -161.25) * mm});
            skLineSegment(sketch, "E948", {"start": v(-76.2, -161.25) * mm, "end": v(50.8, -161.25) * mm});
            skLineSegment(sketch, "E949", {"start": v(50.8, -168.8) * mm, "end": v(76.2, -168.8) * mm});
            skLineSegment(sketch, "E950", {"start": v(-76.2, -168.8) * mm, "end": v(50.8, -168.8) * mm});
            skLineSegment(sketch, "E951", {"start": v(50.8, -176.34) * mm, "end": v(76.2, -176.34) * mm});
            skLineSegment(sketch, "E952", {"start": v(-76.2, -176.34) * mm, "end": v(50.8, -176.34) * mm});
            skLineSegment(sketch, "E953", {"start": v(50.8, -183.88) * mm, "end": v(76.2, -183.88) * mm});
            skLineSegment(sketch, "E954", {"start": v(-76.2, -183.88) * mm, "end": v(50.8, -183.88) * mm});
            skLineSegment(sketch, "E955", {"start": v(50.8, -191.43) * mm, "end": v(76.2, -191.43) * mm});
            skLineSegment(sketch, "E956", {"start": v(-76.2, -191.43) * mm, "end": v(50.8, -191.43) * mm});
            skLineSegment(sketch, "E957", {"start": v(50.8, -198.97) * mm, "end": v(76.2, -198.97) * mm});
            skLineSegment(sketch, "E958", {"start": v(-76.2, -198.97) * mm, "end": v(50.8, -198.97) * mm});
            skLineSegment(sketch, "E959", {"start": v(50.8, -206.51) * mm, "end": v(76.2, -206.51) * mm});
            skLineSegment(sketch, "E960", {"start": v(-76.2, -206.51) * mm, "end": v(50.8, -206.51) * mm});
            skLineSegment(sketch, "E961", {"start": v(50.8, -214.06) * mm, "end": v(76.2, -214.06) * mm});
            skLineSegment(sketch, "E962", {"start": v(-76.2, -214.06) * mm, "end": v(50.8, -214.06) * mm});
            skLineSegment(sketch, "E963", {"start": v(50.8, -221.6) * mm, "end": v(76.2, -221.6) * mm});
            skLineSegment(sketch, "E964", {"start": v(-76.2, -221.6) * mm, "end": v(50.8, -221.6) * mm});
            skLineSegment(sketch, "E965", {"start": v(50.8, -229.15) * mm, "end": v(76.2, -229.15) * mm});
            skLineSegment(sketch, "E966", {"start": v(-76.2, -229.15) * mm, "end": v(50.8, -229.15) * mm});
            skLineSegment(sketch, "E967", {"start": v(50.8, -236.7) * mm, "end": v(76.2, -236.7) * mm});
            skLineSegment(sketch, "E968", {"start": v(-76.2, -236.7) * mm, "end": v(50.8, -236.7) * mm});
            skLineSegment(sketch, "E969", {"start": v(50.8, -244.23) * mm, "end": v(76.2, -244.23) * mm});
            skLineSegment(sketch, "E970", {"start": v(-76.2, -244.23) * mm, "end": v(50.8, -244.23) * mm});
            skLineSegment(sketch, "E971", {"start": v(50.8, -251.78) * mm, "end": v(76.2, -251.78) * mm});
            skLineSegment(sketch, "E972", {"start": v(-76.2, -251.78) * mm, "end": v(50.8, -251.78) * mm});
            skLineSegment(sketch, "E973", {"start": v(50.8, -259.32) * mm, "end": v(76.2, -259.32) * mm});
            skLineSegment(sketch, "E974", {"start": v(-76.2, -259.32) * mm, "end": v(50.8, -259.32) * mm});
            skLineSegment(sketch, "E975", {"start": v(50.8, -266.87) * mm, "end": v(76.2, -266.87) * mm});
            skLineSegment(sketch, "E976", {"start": v(-76.2, -266.87) * mm, "end": v(50.8, -266.87) * mm});
            skLineSegment(sketch, "E977", {"start": v(50.8, -274.4) * mm, "end": v(76.2, -274.4) * mm});
            skLineSegment(sketch, "E978", {"start": v(-76.2, -274.4) * mm, "end": v(50.8, -274.4) * mm});
            skLineSegment(sketch, "E979", {"start": v(50.8, -281.95) * mm, "end": v(76.2, -281.95) * mm});
            skLineSegment(sketch, "E980", {"start": v(-76.2, -281.95) * mm, "end": v(50.8, -281.95) * mm});
            skLineSegment(sketch, "E981", {"start": v(50.8, -289.5) * mm, "end": v(76.2, -289.5) * mm});
            skLineSegment(sketch, "E982", {"start": v(-76.2, -289.5) * mm, "end": v(50.8, -289.5) * mm});
            skLineSegment(sketch, "E983", {"start": v(50.8, -297.04) * mm, "end": v(76.2, -297.04) * mm});
            skLineSegment(sketch, "E984", {"start": v(-76.2, -297.04) * mm, "end": v(50.8, -297.04) * mm});
            skLineSegment(sketch, "E985", {"start": v(50.8, -304.58) * mm, "end": v(76.2, -304.58) * mm});
            skLineSegment(sketch, "E986", {"start": v(-76.2, -304.58) * mm, "end": v(50.8, -304.58) * mm});
            skLineSegment(sketch, "E987", {"start": v(50.8, -312.13) * mm, "end": v(76.2, -312.13) * mm});
            skLineSegment(sketch, "E988", {"start": v(-76.2, -312.13) * mm, "end": v(50.8, -312.13) * mm});
            skLineSegment(sketch, "E989", {"start": v(50.8, -319.67) * mm, "end": v(76.2, -319.67) * mm});
            skLineSegment(sketch, "E990", {"start": v(-76.2, -319.67) * mm, "end": v(50.8, -319.67) * mm});
            skLineSegment(sketch, "E991", {"start": v(50.8, -327.22) * mm, "end": v(76.2, -327.22) * mm});
            skLineSegment(sketch, "E992", {"start": v(-76.2, -327.22) * mm, "end": v(50.8, -327.22) * mm});
            skLineSegment(sketch, "E993", {"start": v(50.8, -334.76) * mm, "end": v(76.2, -334.76) * mm});
            skLineSegment(sketch, "E994", {"start": v(-76.2, -334.76) * mm, "end": v(50.8, -334.76) * mm});
            skLineSegment(sketch, "E995", {"start": v(50.8, -342.3) * mm, "end": v(76.2, -342.3) * mm});
            skLineSegment(sketch, "E996", {"start": v(-76.2, -342.3) * mm, "end": v(50.8, -342.3) * mm});
            skLineSegment(sketch, "E997", {"start": v(50.8, -349.85) * mm, "end": v(76.2, -349.85) * mm});
            skLineSegment(sketch, "E998", {"start": v(-76.2, -349.85) * mm, "end": v(50.8, -349.85) * mm});
            skLineSegment(sketch, "E999", {"start": v(50.8, -357.4) * mm, "end": v(76.2, -357.4) * mm});
            skLineSegment(sketch, "E1000", {"start": v(-76.2, -357.4) * mm, "end": v(50.8, -357.4) * mm});
            skLineSegment(sketch, "E1001", {"start": v(50.8, -364.93) * mm, "end": v(76.2, -364.93) * mm});
            skLineSegment(sketch, "E1002", {"start": v(-76.2, -364.93) * mm, "end": v(50.8, -364.93) * mm});
            skLineSegment(sketch, "E1003", {"start": v(50.8, -372.48) * mm, "end": v(76.2, -372.48) * mm});
            skLineSegment(sketch, "E1004", {"start": v(-76.2, -372.48) * mm, "end": v(50.8, -372.48) * mm});
            skLineSegment(sketch, "E1005", {"start": v(50.8, -380.02) * mm, "end": v(76.2, -380.02) * mm});
            skLineSegment(sketch, "E1006", {"start": v(-76.2, -380.02) * mm, "end": v(50.8, -380.02) * mm});
            skLineSegment(sketch, "E1007", {"start": v(50.8, -387.57) * mm, "end": v(76.2, -387.57) * mm});
            skLineSegment(sketch, "E1008", {"start": v(-76.2, -387.57) * mm, "end": v(50.8, -387.57) * mm});
            skLineSegment(sketch, "E1009", {"start": v(50.8, -395.1) * mm, "end": v(76.2, -395.1) * mm});
            skLineSegment(sketch, "E1010", {"start": v(-76.2, -395.1) * mm, "end": v(50.8, -395.1) * mm});
            skLineSegment(sketch, "E1011", {"start": v(50.8, -402.65) * mm, "end": v(76.2, -402.65) * mm});
            skLineSegment(sketch, "E1012", {"start": v(-76.2, -402.65) * mm, "end": v(50.8, -402.65) * mm});
            skLineSegment(sketch, "E1013", {"start": v(50.8, -410.2) * mm, "end": v(76.2, -410.2) * mm});
            skLineSegment(sketch, "E1014", {"start": v(-76.2, -410.2) * mm, "end": v(50.8, -410.2) * mm});
            skLineSegment(sketch, "E1015", {"start": v(50.8, -417.74) * mm, "end": v(76.2, -417.74) * mm});
            skLineSegment(sketch, "E1016", {"start": v(-76.2, -417.74) * mm, "end": v(50.8, -417.74) * mm});
            skLineSegment(sketch, "E1017", {"start": v(76.2, -424.6) * mm, "end": v(1003.85, -424.6) * mm});
            skLineSegment(sketch, "E1018", {"start": v(1003.85, -424.6) * mm, "end": v(1156.25, -424.6) * mm});
            skLineSegment(sketch, "E1019", {"start": v(1156.25, -424.6) * mm, "end": v(303.1, 261.2) * mm});
            skLineSegment(sketch, "E1020", {"start": v(-1003.85, -424.6) * mm, "end": v(-1156.25, -424.6) * mm});
            skLineSegment(sketch, "E1021", {"start": v(-1156.25, -424.6) * mm, "end": v(-303.1, 261.2) * mm});
            skSolve(sketch);
        }
        {
            var Q0;
            Q0=qCreatedBy(makeId("Front.planeOp"),FACE);
            var sketch = newSketch(context, id + "F2", { "sketchPlane" : qUnion([Q0])});
            skLineSegment(sketch, "E1022.0", {"start": v(-1003.85, -424.6) * mm, "end": v(76.2, -424.6) * mm});
            skLineSegment(sketch, "E1022.1", {"start": v(-959.85, -348.4) * mm, "end": v(-1003.85, -424.6) * mm});
            skLineSegment(sketch, "E1022.2", {"start": v(-959.85, -348.4) * mm, "end": v(-921.75, -348.4) * mm});
            skLineSegment(sketch, "E1022.3", {"start": v(-877.76, -272.2) * mm, "end": v(-921.75, -348.4) * mm});
            skLineSegment(sketch, "E1022.4", {"start": v(-877.76, -272.2) * mm, "end": v(-839.66, -272.2) * mm});
            skLineSegment(sketch, "E1022.5", {"start": v(-795.66, -196) * mm, "end": v(-839.66, -272.2) * mm});
            skLineSegment(sketch, "E1022.6", {"start": v(-795.66, -196) * mm, "end": v(-757.56, -196) * mm});
            skLineSegment(sketch, "E1022.7", {"start": v(-713.57, -119.8) * mm, "end": v(-757.56, -196) * mm});
            skLineSegment(sketch, "E1022.8", {"start": v(-713.57, -119.8) * mm, "end": v(-675.47, -119.8) * mm});
            skLineSegment(sketch, "E1022.9", {"start": v(-631.47, -43.6) * mm, "end": v(-675.47, -119.8) * mm});
            skLineSegment(sketch, "E1022.10", {"start": v(-631.47, -43.6) * mm, "end": v(-593.37, -43.6) * mm});
            skLineSegment(sketch, "E1022.11", {"start": v(-549.38, 32.6) * mm, "end": v(-593.37, -43.6) * mm});
            skLineSegment(sketch, "E1022.12", {"start": v(-549.38, 32.6) * mm, "end": v(-511.28, 32.6) * mm});
            skLineSegment(sketch, "E1022.13", {"start": v(-467.29, 108.8) * mm, "end": v(-511.28, 32.6) * mm});
            skLineSegment(sketch, "E1022.14", {"start": v(-467.29, 108.8) * mm, "end": v(-429.19, 108.8) * mm});
            skLineSegment(sketch, "E1022.15", {"start": v(-385.2, 185) * mm, "end": v(-429.19, 108.8) * mm});
            skLineSegment(sketch, "E1022.16", {"start": v(-385.2, 185) * mm, "end": v(-347.1, 185) * mm});
            skLineSegment(sketch, "E1022.17", {"start": v(-303.1, 261.2) * mm, "end": v(-347.1, 185) * mm});
            skLineSegment(sketch, "E1022.18", {"start": v(-303.1, 261.2) * mm, "end": v(-265, 261.2) * mm});
            skLineSegment(sketch, "E1022.19", {"start": v(-265, 261.2) * mm, "end": v(265, 261.2) * mm});
            skLineSegment(sketch, "E1022.20", {"start": v(303.1, 261.2) * mm, "end": v(265, 261.2) * mm});
            skLineSegment(sketch, "E1022.21", {"start": v(303.1, 261.2) * mm, "end": v(347.1, 185) * mm});
            skLineSegment(sketch, "E1022.22", {"start": v(347.1, 185) * mm, "end": v(385.2, 185) * mm});
            skLineSegment(sketch, "E1022.23", {"start": v(385.2, 185) * mm, "end": v(429.19, 108.8) * mm});
            skLineSegment(sketch, "E1022.25", {"start": v(467.29, 108.8) * mm, "end": v(511.28, 32.6) * mm});
            skLineSegment(sketch, "E1022.26", {"start": v(511.28, 32.6) * mm, "end": v(549.38, 32.6) * mm});
            skLineSegment(sketch, "E1022.27", {"start": v(549.38, 32.6) * mm, "end": v(593.37, -43.6) * mm});
            skLineSegment(sketch, "E1022.28", {"start": v(593.37, -43.6) * mm, "end": v(631.47, -43.6) * mm});
            skLineSegment(sketch, "E1022.29", {"start": v(631.47, -43.6) * mm, "end": v(675.47, -119.8) * mm});
            skLineSegment(sketch, "E1022.30", {"start": v(675.47, -119.8) * mm, "end": v(713.57, -119.8) * mm});
            skLineSegment(sketch, "E1022.31", {"start": v(713.57, -119.8) * mm, "end": v(757.56, -196) * mm});
            skLineSegment(sketch, "E1022.32", {"start": v(757.56, -196) * mm, "end": v(795.66, -196) * mm});
            skLineSegment(sketch, "E1022.33", {"start": v(795.66, -196) * mm, "end": v(839.66, -272.2) * mm});
            skLineSegment(sketch, "E1022.34", {"start": v(839.66, -272.2) * mm, "end": v(877.76, -272.2) * mm});
            skLineSegment(sketch, "E1022.35", {"start": v(877.76, -272.2) * mm, "end": v(921.75, -348.4) * mm});
            skLineSegment(sketch, "E1022.36", {"start": v(921.75, -348.4) * mm, "end": v(959.85, -348.4) * mm});
            skLineSegment(sketch, "E1022.37", {"start": v(959.85, -348.4) * mm, "end": v(1003.85, -424.6) * mm});
            skLineSegment(sketch, "E1022.38", {"start": v(76.2, -424.6) * mm, "end": v(1003.85, -424.6) * mm});
            skPoint(sketch, "E1022.24.end.orphan", {"position": v(467.29, 108.8) * mm});
            skLineSegment(sketch, "E1023", {"start": v(429.19, 108.8) * mm, "end": v(467.29, 108.8) * mm});
            skSolve(sketch);
        }
        {
            var Q0;
            Q0=makeQuery(id+"F2.imprint","IMPRINT",FACE,{"disambiguationData":[TD([[makeQuery(id+"F2.imprint","IMPRINT",EDGE,{"derivedFrom":sQuery(id+"F2.wireOp",EDGE,"E1022.0")}),1.0]])]});
            extrude(context, id + "F3", {"entities" : qUnion([Q0]), "endBound" : BoundingType.SYMMETRIC, "depth" : 2007.7 * mm, "offsetDistance" : 25.4 * mm});
        }
        {
            var Q0;
            Q0=qCreatedBy(makeId("Right.planeOp"),FACE);
            var sketch = newSketch(context, id + "F4", { "sketchPlane" : qUnion([Q0])});
            skLineSegment(sketch, "E1024.0", {"start": v(76.2, -424.6) * mm, "end": v(1003.85, -424.6) * mm});
            skLineSegment(sketch, "E1024.1", {"start": v(959.85, -348.4) * mm, "end": v(1003.85, -424.6) * mm});
            skLineSegment(sketch, "E1024.2", {"start": v(921.75, -348.4) * mm, "end": v(959.85, -348.4) * mm});
            skLineSegment(sketch, "E1024.3", {"start": v(877.76, -272.2) * mm, "end": v(921.75, -348.4) * mm});
            skLineSegment(sketch, "E1024.4", {"start": v(839.66, -272.2) * mm, "end": v(877.76, -272.2) * mm});
            skLineSegment(sketch, "E1024.5", {"start": v(795.66, -196) * mm, "end": v(839.66, -272.2) * mm});
            skLineSegment(sketch, "E1024.7", {"start": v(713.57, -119.8) * mm, "end": v(757.56, -196) * mm});
            skLineSegment(sketch, "E1024.8", {"start": v(675.47, -119.8) * mm, "end": v(713.57, -119.8) * mm});
            skLineSegment(sketch, "E1024.9", {"start": v(631.47, -43.6) * mm, "end": v(675.47, -119.8) * mm});
            skLineSegment(sketch, "E1024.11", {"start": v(549.38, 32.6) * mm, "end": v(593.37, -43.6) * mm});
            skLineSegment(sketch, "E1024.12", {"start": v(511.28, 32.6) * mm, "end": v(549.38, 32.6) * mm});
            skLineSegment(sketch, "E1024.13", {"start": v(467.29, 108.8) * mm, "end": v(511.28, 32.6) * mm});
            skLineSegment(sketch, "E1024.14", {"start": v(429.19, 108.8) * mm, "end": v(467.29, 108.8) * mm});
            skLineSegment(sketch, "E1024.15", {"start": v(385.2, 185) * mm, "end": v(429.19, 108.8) * mm});
            skLineSegment(sketch, "E1024.16", {"start": v(347.1, 185) * mm, "end": v(385.2, 185) * mm});
            skLineSegment(sketch, "E1024.17", {"start": v(303.1, 261.2) * mm, "end": v(347.1, 185) * mm});
            skLineSegment(sketch, "E1024.18", {"start": v(303.1, 261.2) * mm, "end": v(265, 261.2) * mm});
            skLineSegment(sketch, "E1024.19", {"start": v(-265, 261.2) * mm, "end": v(265, 261.2) * mm});
            skLineSegment(sketch, "E1024.20", {"start": v(-303.1, 261.2) * mm, "end": v(-265, 261.2) * mm});
            skLineSegment(sketch, "E1024.21", {"start": v(-303.1, 261.2) * mm, "end": v(-347.1, 185) * mm});
            skLineSegment(sketch, "E1024.23", {"start": v(-385.2, 185) * mm, "end": v(-429.19, 108.8) * mm});
            skLineSegment(sketch, "E1024.25", {"start": v(-467.29, 108.8) * mm, "end": v(-511.28, 32.6) * mm});
            skLineSegment(sketch, "E1024.27", {"start": v(-549.38, 32.6) * mm, "end": v(-593.37, -43.6) * mm});
            skLineSegment(sketch, "E1024.29", {"start": v(-631.47, -43.6) * mm, "end": v(-675.47, -119.8) * mm});
            skLineSegment(sketch, "E1024.31", {"start": v(-713.57, -119.8) * mm, "end": v(-757.56, -196) * mm});
            skLineSegment(sketch, "E1024.32", {"start": v(-795.66, -196) * mm, "end": v(-757.56, -196) * mm});
            skLineSegment(sketch, "E1024.33", {"start": v(-795.66, -196) * mm, "end": v(-839.66, -272.2) * mm});
            skLineSegment(sketch, "E1024.35", {"start": v(-877.76, -272.2) * mm, "end": v(-921.75, -348.4) * mm});
            skLineSegment(sketch, "E1024.36", {"start": v(-959.85, -348.4) * mm, "end": v(-921.75, -348.4) * mm});
            skLineSegment(sketch, "E1024.37", {"start": v(-959.85, -348.4) * mm, "end": v(-1003.85, -424.6) * mm});
            skLineSegment(sketch, "E1024.38", {"start": v(-1003.85, -424.6) * mm, "end": v(76.2, -424.6) * mm});
            skPoint(sketch, "E1024.10.end.orphan", {"position": v(631.47, -43.6) * mm});
            skPoint(sketch, "E1024.6.end.orphan", {"position": v(795.66, -196) * mm});
            skPoint(sketch, "E1024.34.start.orphan", {"position": v(-877.76, -272.2) * mm});
            skPoint(sketch, "E1024.30.start.orphan", {"position": v(-713.57, -119.8) * mm});
            skPoint(sketch, "E1024.28.start.orphan", {"position": v(-631.47, -43.6) * mm});
            skPoint(sketch, "E1024.26.start.orphan", {"position": v(-549.38, 32.6) * mm});
            skPoint(sketch, "E1024.24.start.orphan", {"position": v(-467.29, 108.8) * mm});
            skPoint(sketch, "E1024.22.start.orphan", {"position": v(-385.2, 185) * mm});
            skLineSegment(sketch, "E1025", {"start": v(-347.1, 185) * mm, "end": v(-385.2, 185) * mm});
            skLineSegment(sketch, "E1026", {"start": v(-429.19, 108.8) * mm, "end": v(-467.29, 108.8) * mm});
            skLineSegment(sketch, "E1027", {"start": v(-511.28, 32.6) * mm, "end": v(-549.38, 32.6) * mm});
            skLineSegment(sketch, "E1028", {"start": v(-593.37, -43.6) * mm, "end": v(-631.47, -43.6) * mm});
            skLineSegment(sketch, "E1029", {"start": v(-675.47, -119.8) * mm, "end": v(-713.57, -119.8) * mm});
            skLineSegment(sketch, "E1030", {"start": v(-839.66, -272.2) * mm, "end": v(-877.76, -272.2) * mm});
            skLineSegment(sketch, "E1031", {"start": v(593.37, -43.6) * mm, "end": v(631.47, -43.6) * mm});
            skLineSegment(sketch, "E1032", {"start": v(757.56, -196) * mm, "end": v(795.66, -196) * mm});
            skLineSegment(sketch, "E1033.bottom", {"start": v(1235.19, 470.62) * mm, "end": v(-1313.54, 470.62) * mm});
            skLineSegment(sketch, "E1033.top", {"start": v(1235.19, -782.62) * mm, "end": v(-1313.54, -782.62) * mm});
            skLineSegment(sketch, "E1033.left", {"start": v(1235.19, 470.62) * mm, "end": v(1235.19, -782.62) * mm});
            skLineSegment(sketch, "E1033.right", {"start": v(-1313.54, 470.62) * mm, "end": v(-1313.54, -782.62) * mm});
            skSolve(sketch);
        }
        {
            var Q0;
            Q0 = qSketchRegion(id + "F4", true);
            extrude(context, id + "F5", {"entities" : qUnion([Q0]), "operationType" : NewBodyOperationType.REMOVE, "endBound" : BoundingType.SYMMETRIC, "oppositeDirection" : true, "depth" : 2007.7 * mm, "offsetDistance" : 25.4 * mm});
        }
        {
            var Q0;
            Q0=qCreatedBy(makeId("Front.planeOp"),FACE);
            var sketch = newSketch(context, id + "F6", { "sketchPlane" : qUnion([Q0])});
            skLineSegment(sketch, "E1034.13", {"start": v(273.05, 424.6) * mm, "end": v(-273.05, 424.6) * mm});
            skLineSegment(sketch, "E1034.24", {"start": v(-265, 261.2) * mm, "end": v(265, 261.2) * mm});
            skLineSegment(sketch, "E1035", {"start": v(273.05, 424.6) * mm, "end": v(273.05, 261.2) * mm});
            skLineSegment(sketch, "E1036", {"start": v(273.05, 261.2) * mm, "end": v(265, 261.2) * mm});
            skLineSegment(sketch, "E1037", {"start": v(-273.05, 424.6) * mm, "end": v(-273.05, 261.2) * mm});
            skLineSegment(sketch, "E1038", {"start": v(-273.05, 261.2) * mm, "end": v(-265, 261.2) * mm});
            skSolve(sketch);
        }
        {
            var Q0;
            Q0=qCreatedBy(makeId("Right.planeOp"),FACE);
            var sketch = newSketch(context, id + "F7", { "sketchPlane" : qUnion([Q0])});
            skLineSegment(sketch, "E1039.0", {"start": v(-255.7, 277.3) * mm, "end": v(-265, 261.2) * mm});
            skArc(sketch, "E1039.1", {"start": v(-255.7, 277.3) * mm, "mid": v(-254.43, 280.37) * mm, "end": v(-254, 283.65) * mm});
            skLineSegment(sketch, "E1039.2", {"start": v(-254, 324.48) * mm, "end": v(-254, 283.65) * mm});
            skLineSegment(sketch, "E1039.3", {"start": v(-266.7, 324.48) * mm, "end": v(-254, 324.48) * mm});
            skLineSegment(sketch, "E1039.4", {"start": v(-266.7, 354.13) * mm, "end": v(-266.7, 324.48) * mm});
            skLineSegment(sketch, "E1039.5", {"start": v(-266.7, 354.13) * mm, "end": v(-266.7, 363.24) * mm});
            skLineSegment(sketch, "E1039.6", {"start": v(-266.7, 363.24) * mm, "end": v(-254, 363.24) * mm});
            skLineSegment(sketch, "E1039.7", {"start": v(-254, 387.76) * mm, "end": v(-254, 363.24) * mm});
            skLineSegment(sketch, "E1039.8", {"start": v(-266.7, 387.76) * mm, "end": v(-254, 387.76) * mm});
            skLineSegment(sketch, "E1039.9", {"start": v(-266.7, 387.76) * mm, "end": v(-266.7, 404.49) * mm});
            skLineSegment(sketch, "E1039.10", {"start": v(-266.7, 404.49) * mm, "end": v(-266.7, 411.9) * mm});
            skArc(sketch, "E1039.11", {"start": v(-266.7, 411.9) * mm, "mid": v(-266.92, 413.54) * mm, "end": v(-267.55, 415.07) * mm});
            skLineSegment(sketch, "E1039.12", {"start": v(-267.55, 415.07) * mm, "end": v(-273.05, 424.6) * mm});
            skLineSegment(sketch, "E1039.13", {"start": v(273.05, 424.6) * mm, "end": v(-273.05, 424.6) * mm});
            skLineSegment(sketch, "E1039.14", {"start": v(267.55, 415.07) * mm, "end": v(273.05, 424.6) * mm});
            skArc(sketch, "E1039.15", {"start": v(267.55, 415.07) * mm, "mid": v(266.92, 413.54) * mm, "end": v(266.7, 411.9) * mm});
            skLineSegment(sketch, "E1039.16", {"start": v(266.7, 404.49) * mm, "end": v(266.7, 411.9) * mm});
            skLineSegment(sketch, "E1039.17", {"start": v(266.7, 387.76) * mm, "end": v(266.7, 404.49) * mm});
            skLineSegment(sketch, "E1039.18", {"start": v(254, 363.24) * mm, "end": v(254, 387.76) * mm});
            skLineSegment(sketch, "E1039.19", {"start": v(266.7, 354.13) * mm, "end": v(266.7, 363.24) * mm});
            skLineSegment(sketch, "E1039.20", {"start": v(266.7, 354.13) * mm, "end": v(266.7, 324.48) * mm});
            skLineSegment(sketch, "E1039.21", {"start": v(254, 283.65) * mm, "end": v(254, 324.48) * mm});
            skArc(sketch, "E1039.22", {"start": v(254, 283.65) * mm, "mid": v(254.43, 280.37) * mm, "end": v(255.7, 277.3) * mm});
            skLineSegment(sketch, "E1039.23", {"start": v(255.7, 277.3) * mm, "end": v(265, 261.2) * mm});
            skLineSegment(sketch, "E1039.24", {"start": v(-265, 261.2) * mm, "end": v(265, 261.2) * mm});
            skLineSegment(sketch, "E1040.trimOffspring", {"start": v(254, 387.76) * mm, "end": v(266.7, 387.76) * mm});
            skLineSegment(sketch, "E1041.trimOffspring", {"start": v(254, 363.24) * mm, "end": v(266.7, 363.24) * mm});
            skLineSegment(sketch, "E1042.trimOffspring", {"start": v(254, 324.48) * mm, "end": v(266.7, 324.48) * mm});
            skSolve(sketch);
        }
        {
            var Q0;
            Q0 = qSketchRegion(id + "F6", true);
            extrude(context, id + "F8", {"entities" : qUnion([Q0]), "operationType" : NewBodyOperationType.ADD, "endBound" : BoundingType.SYMMETRIC, "depth" : 546.1 * mm, "offsetDistance" : 25.4 * mm});
        }
        {
            var Q0;
            Q0=makeQuery(id+"F8.opExtrude","SWEPT_FACE",FACE,{"disambiguationData":[OSD([sQuery(id+"F6.wireOp",EDGE,"E1035")])]});
            var sketch = newSketch(context, id + "F9", { "sketchPlane" : qUnion([Q0])});
            skLineSegment(sketch, "E1043.0", {"start": v(267.55, 415.07) * mm, "end": v(273.05, 424.6) * mm});
            skArc(sketch, "E1043.1", {"start": v(267.55, 415.07) * mm, "mid": v(266.92, 413.54) * mm, "end": v(266.7, 411.9) * mm});
            skLineSegment(sketch, "E1043.2", {"start": v(266.7, 404.49) * mm, "end": v(266.7, 411.9) * mm});
            skLineSegment(sketch, "E1043.3", {"start": v(266.7, 387.76) * mm, "end": v(266.7, 404.49) * mm});
            skLineSegment(sketch, "E1043.4", {"start": v(254, 387.76) * mm, "end": v(266.7, 387.76) * mm});
            skLineSegment(sketch, "E1043.5", {"start": v(254, 363.24) * mm, "end": v(254, 387.76) * mm});
            skLineSegment(sketch, "E1043.6", {"start": v(254, 363.24) * mm, "end": v(266.7, 363.24) * mm});
            skLineSegment(sketch, "E1043.7", {"start": v(266.7, 354.13) * mm, "end": v(266.7, 363.24) * mm});
            skLineSegment(sketch, "E1043.8", {"start": v(266.7, 354.13) * mm, "end": v(266.7, 324.48) * mm});
            skLineSegment(sketch, "E1043.9", {"start": v(254, 324.48) * mm, "end": v(266.7, 324.48) * mm});
            skLineSegment(sketch, "E1043.10", {"start": v(254, 283.65) * mm, "end": v(254, 324.48) * mm});
            skLineSegment(sketch, "E1043.11", {"start": v(255.7, 277.3) * mm, "end": v(265, 261.2) * mm});
            skArc(sketch, "E1043.12", {"start": v(254, 283.65) * mm, "mid": v(254.43, 280.37) * mm, "end": v(255.7, 277.3) * mm});
            skPoint(sketch, "E1043.13", {"position": v(266.7, 408.2) * mm});
            skLineSegment(sketch, "E1044.0", {"start": v(-255.7, 277.3) * mm, "end": v(-265, 261.2) * mm});
            skArc(sketch, "E1044.1", {"start": v(-255.7, 277.3) * mm, "mid": v(-254.43, 280.37) * mm, "end": v(-254, 283.65) * mm});
            skLineSegment(sketch, "E1044.2", {"start": v(-254, 324.48) * mm, "end": v(-254, 283.65) * mm});
            skLineSegment(sketch, "E1044.3", {"start": v(-266.7, 324.48) * mm, "end": v(-254, 324.48) * mm});
            skLineSegment(sketch, "E1044.4", {"start": v(-266.7, 354.13) * mm, "end": v(-266.7, 324.48) * mm});
            skLineSegment(sketch, "E1044.5", {"start": v(-266.7, 354.13) * mm, "end": v(-266.7, 363.24) * mm});
            skLineSegment(sketch, "E1044.6", {"start": v(-266.7, 363.24) * mm, "end": v(-254, 363.24) * mm});
            skLineSegment(sketch, "E1044.7", {"start": v(-254, 387.76) * mm, "end": v(-254, 363.24) * mm});
            skLineSegment(sketch, "E1044.8", {"start": v(-266.7, 387.76) * mm, "end": v(-254, 387.76) * mm});
            skLineSegment(sketch, "E1044.9", {"start": v(-266.7, 387.76) * mm, "end": v(-266.7, 404.49) * mm});
            skLineSegment(sketch, "E1044.10", {"start": v(-266.7, 404.49) * mm, "end": v(-266.7, 411.9) * mm});
            skLineSegment(sketch, "E1044.11", {"start": v(-267.55, 415.07) * mm, "end": v(-273.05, 424.6) * mm});
            skArc(sketch, "E1044.12", {"start": v(-266.7, 411.9) * mm, "mid": v(-266.92, 413.54) * mm, "end": v(-267.55, 415.07) * mm});
            skLineSegment(sketch, "E1045", {"start": v(-273.05, 424.6) * mm, "end": v(-273.05, 261.2) * mm});
            skLineSegment(sketch, "E1046", {"start": v(-273.05, 261.2) * mm, "end": v(-265, 261.2) * mm});
            skLineSegment(sketch, "E1047", {"start": v(273.05, 424.6) * mm, "end": v(273.05, 261.2) * mm});
            skLineSegment(sketch, "E1048", {"start": v(273.05, 261.2) * mm, "end": v(265, 261.2) * mm});
            skSolve(sketch);
        }
        {
            var Q0;
            Q0 = qSketchRegion(id + "F9", true);
            var Q1;
            Q1=makeQuery(id+"F8.opExtrude","SWEPT_FACE",FACE,{"disambiguationData":[OSD([sQuery(id+"F6.wireOp",EDGE,"E1037")])]});
            extrude(context, id + "F10", {"entities" : qUnion([Q0]), "operationType" : NewBodyOperationType.REMOVE, "endBound" : BoundingType.UP_TO_SURFACE, "oppositeDirection" : true, "depth" : 546.1 * mm, "endBoundEntityFace" : qUnion([Q1]), "offsetDistance" : 25.4 * mm});
        }
        {
            var Q0;
            Q0=qCreatedBy(makeId("Front.planeOp"),FACE);
            var sketch = newSketch(context, id + "F11", { "sketchPlane" : qUnion([Q0])});
            skLineSegment(sketch, "E1049.0", {"start": v(255.7, 277.3) * mm, "end": v(265, 261.2) * mm});
            skArc(sketch, "E1049.1", {"start": v(254, 283.65) * mm, "mid": v(254.43, 280.37) * mm, "end": v(255.7, 277.3) * mm});
            skLineSegment(sketch, "E1049.2", {"start": v(254, 283.65) * mm, "end": v(254, 324.48) * mm});
            skLineSegment(sketch, "E1049.3", {"start": v(266.7, 354.13) * mm, "end": v(266.7, 324.48) * mm});
            skLineSegment(sketch, "E1049.4", {"start": v(266.7, 354.13) * mm, "end": v(266.7, 363.24) * mm});
            skLineSegment(sketch, "E1049.5", {"start": v(254, 363.24) * mm, "end": v(254, 387.76) * mm});
            skLineSegment(sketch, "E1049.6", {"start": v(266.7, 387.76) * mm, "end": v(266.7, 404.49) * mm});
            skLineSegment(sketch, "E1049.7", {"start": v(266.7, 404.49) * mm, "end": v(266.7, 411.9) * mm});
            skArc(sketch, "E1049.8", {"start": v(267.55, 415.07) * mm, "mid": v(266.92, 413.54) * mm, "end": v(266.7, 411.9) * mm});
            skLineSegment(sketch, "E1049.9", {"start": v(267.55, 415.07) * mm, "end": v(273.05, 424.6) * mm});
            skLineSegment(sketch, "E1049.10", {"start": v(-267.55, 415.07) * mm, "end": v(-273.05, 424.6) * mm});
            skArc(sketch, "E1049.11", {"start": v(-266.7, 411.9) * mm, "mid": v(-266.92, 413.54) * mm, "end": v(-267.55, 415.07) * mm});
            skLineSegment(sketch, "E1049.12", {"start": v(-266.7, 404.49) * mm, "end": v(-266.7, 411.9) * mm});
            skLineSegment(sketch, "E1049.13", {"start": v(-266.7, 387.76) * mm, "end": v(-266.7, 404.49) * mm});
            skLineSegment(sketch, "E1049.14", {"start": v(-254, 387.76) * mm, "end": v(-254, 363.24) * mm});
            skLineSegment(sketch, "E1049.15", {"start": v(-266.7, 354.13) * mm, "end": v(-266.7, 363.24) * mm});
            skLineSegment(sketch, "E1049.16", {"start": v(-266.7, 354.13) * mm, "end": v(-266.7, 324.48) * mm});
            skLineSegment(sketch, "E1049.17", {"start": v(-254, 324.48) * mm, "end": v(-254, 283.65) * mm});
            skArc(sketch, "E1049.18", {"start": v(-255.7, 277.3) * mm, "mid": v(-254.43, 280.37) * mm, "end": v(-254, 283.65) * mm});
            skLineSegment(sketch, "E1049.19", {"start": v(-255.7, 277.3) * mm, "end": v(-265, 261.2) * mm});
            skPoint(sketch, "E1050.0", {"position": v(-273.05, 261.2) * mm});
            skPoint(sketch, "E1050.1", {"position": v(273.05, 261.2) * mm});
            skLineSegment(sketch, "E1051", {"start": v(273.05, 424.6) * mm, "end": v(273.05, 261.2) * mm});
            skLineSegment(sketch, "E1052", {"start": v(266.7, 324.48) * mm, "end": v(254, 324.48) * mm});
            skLineSegment(sketch, "E1053", {"start": v(266.7, 363.24) * mm, "end": v(254, 363.24) * mm});
            skLineSegment(sketch, "E1054", {"start": v(266.7, 387.76) * mm, "end": v(254, 387.76) * mm});
            skLineSegment(sketch, "E1055", {"start": v(265, 261.2) * mm, "end": v(273.05, 261.2) * mm});
            skLineSegment(sketch, "E1056", {"start": v(-265, 261.2) * mm, "end": v(-273.05, 261.2) * mm});
            skLineSegment(sketch, "E1057", {"start": v(-273.05, 428.66) * mm, "end": v(-273.05, 261.2) * mm});
            skLineSegment(sketch, "E1058", {"start": v(-266.7, 324.48) * mm, "end": v(-254, 324.48) * mm});
            skLineSegment(sketch, "E1059", {"start": v(-266.7, 363.24) * mm, "end": v(-254, 363.24) * mm});
            skLineSegment(sketch, "E1060", {"start": v(-266.7, 387.76) * mm, "end": v(-254, 387.76) * mm});
            skSolve(sketch);
        }
        {
            var Q0;
            Q0 = qSketchRegion(id + "F11", true);
            extrude(context, id + "F12", {"entities" : qUnion([Q0]), "operationType" : NewBodyOperationType.REMOVE, "endBound" : BoundingType.SYMMETRIC, "oppositeDirection" : true, "depth" : 546.1 * mm, "offsetDistance" : 25.4 * mm});
        }
    });
